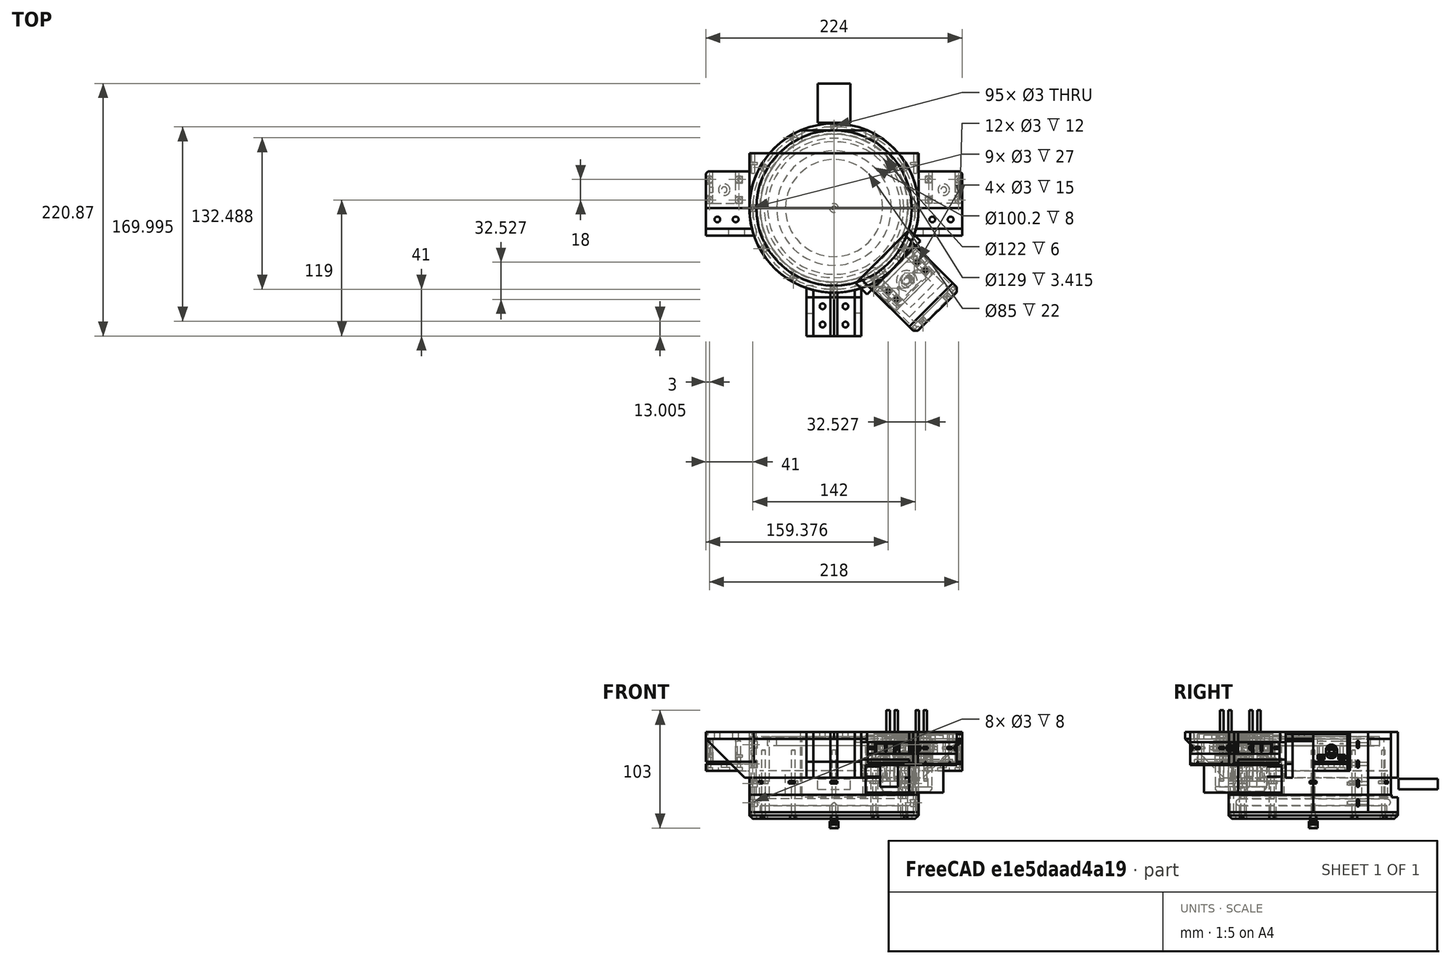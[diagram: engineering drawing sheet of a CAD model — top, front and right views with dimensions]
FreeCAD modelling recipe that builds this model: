
FCSTD DOCUMENT  (FreeCAD 0.19R24276 (Git))
Label: bazovina-part-H_turret-hole_049
License: All rights reserved
LicenseURL: http://en.wikipedia.org/wiki/All_rights_reserved
objects: Part::Cylinder×214, Part::Box×127, Part::Compound×119, Part::Cut×112, Part::Chamfer×32, Mesh::Feature×26, Part::FeaturePython×13, Part::Mirroring×4, Part::Common×2, Part::Torus×1
note: 624 computed .brp shape members not serialized (recipe doc carries the construction recipe); baked Part::Feature solids carry a one-line shape summary decoded from their .brp

FEATURE [Part::Box] Box485  label="Krychle485"
  AttacherType = Attacher::AttachEngine3D
  Height = 49
  Length = 56
  Placement = pos=(-28,35,29) rot=(0,0,1;0rad)
  Width = 200
FEATURE [Part::Box] Box486  label="Krychle486"
  AttacherType = Attacher::AttachEngine3D
  Height = 55
  Length = 148
  Placement = pos=(-74,68,29) rot=(0,0,1;0rad)
  Width = 26
FEATURE [Part::FeaturePython] Tube035  # WARN: FeaturePython — macro-defined, semantics opaque (R4)
  AttacherType = Attacher::AttachEngine3D
  Height = 55
  InnerRadius = 68
  OuterRadius = 74
  Placement = pos=(0,0,29) rot=(0,0,1;0rad)
FEATURE [Part::Cut] Cut455
  Base = -> Tube035
  Tool = -> Box485
FEATURE [Part::Cut] Cut454
  Base = -> Cut455
  Tool = -> Box486
FEATURE [Part::Cylinder] Cylinder971  label="Válec971"
  Angle = 360
  AttacherType = Attacher::AttachEngine3D
  Height = 6
  Placement = pos=(0,0,65) rot=(0,0,1;0rad)
  Radius = 74
FEATURE [Part::Box] Box483  label="Krychle483"
  AttacherType = Attacher::AttachEngine3D
  Height = 34
  Length = 148
  Placement = pos=(-74,68,38) rot=(0,0,1;0rad)
  Width = 20
FEATURE [Part::Cut] Cut453
  Base = -> Cylinder971
  Placement = pos=(0,0,13) rot=(0,0,1;0rad)
  Tool = -> Box483
FEATURE [Part::FeaturePython] Tube036  # WARN: FeaturePython — macro-defined, semantics opaque (R4)
  AttacherType = Attacher::AttachEngine3D
  Height = 8
  InnerRadius = 50.1
  OuterRadius = 58
  Placement = pos=(0,0,72) rot=(0,0,1;0rad)
FEATURE [Part::Box] Box648  label="Krychle648"
  AttacherType = Attacher::AttachEngine3D
  Height = 60
  Length = 200
  Placement = pos=(0,0,-5) rot=(0,0,-1;0.383972rad)
  Width = 200
FEATURE [Part::Box] Box647  label="Krychle647"
  AttacherType = Attacher::AttachEngine3D
  Height = 60
  Length = 200
  Placement = pos=(70.7107,70.7107,-5) rot=(0,0,1;3.92699rad)
  Width = 120
FEATURE [Part::Box] Box649  label="Krychle649"
  AttacherType = Attacher::AttachEngine3D
  Height = 60
  Length = 200
  Placement = pos=(0,0,-5) rot=(0,0,1;3.52556rad)
  Width = 200
FEATURE [Part::Cut] Cut464
  Base = -> Box647
  Tool = -> Box648
FEATURE [Part::Cut] Cut465
  Base = -> Cut464
  Tool = -> Box649
FEATURE [Part::Cut] Cut
  Base = -> Cut454
  Tool = -> Cut465
FEATURE [Part::Cylinder] Cylinder983  label="Válec983"
  Angle = 360
  AttacherType = Attacher::AttachEngine3D
  Height = 60
  Placement = pos=(-61.4878,-35.5,0) rot=(0,0,-1;1.0472rad)
  Radius = 1.5
FEATURE [Part::Cylinder] Cylinder978  label="Válec978"
  Angle = 360
  AttacherType = Attacher::AttachEngine3D
  Height = 60
  Placement = pos=(35.5,61.4878,0) rot=(0,0,1;2.61799rad)
  Radius = 1.5
FEATURE [Part::Cylinder] Cylinder981  label="Válec981"
  Angle = 360
  AttacherType = Attacher::AttachEngine3D
  Height = 60
  Placement = pos=(-61.4878,35.5,0) rot=(0,0,1;4.18879rad)
  Radius = 1.5
FEATURE [Part::Cylinder] Cylinder975  label="Válec975"
  Angle = 360
  AttacherType = Attacher::AttachEngine3D
  Height = 60
  Placement = pos=(61.4878,-35.5,0) rot=(0,0,1;1.0472rad)
  Radius = 1.5
FEATURE [Part::Cylinder] Cylinder986  label="Válec986"
  Angle = 360
  AttacherType = Attacher::AttachEngine3D
  Height = 3
  Placement = pos=(-71,2.7e-14,0) rot=(0,0,-1;1.5708rad)
  Radius = 3
FEATURE [Part::Cylinder] Cylinder980  label="Válec980"
  Angle = 360
  AttacherType = Attacher::AttachEngine3D
  Height = 60
  Placement = pos=(-35.5,61.4878,0) rot=(0,0,1;3.66519rad)
  Radius = 1.5
FEATURE [Part::Cylinder] Cylinder977  label="Válec977"
  Angle = 360
  AttacherType = Attacher::AttachEngine3D
  Height = 60
  Placement = pos=(61.4878,35.5,0) rot=(0,0,1;2.0944rad)
  Radius = 1.5
FEATURE [Part::Cylinder] Cylinder979  label="Válec979"
  Angle = 360
  AttacherType = Attacher::AttachEngine3D
  Height = 60
  Placement = pos=(3.1e-14,71,0) rot=(0,0,1;3.14159rad)
  Radius = 1.5
FEATURE [Part::Cylinder] Cylinder976  label="Válec976"
  Angle = 360
  AttacherType = Attacher::AttachEngine3D
  Height = 60
  Placement = pos=(71,-1.8e-14,0) rot=(0,0,1;1.5708rad)
  Radius = 1.5
FEATURE [Part::Cylinder] Cylinder982  label="Válec982"
  Angle = 360
  AttacherType = Attacher::AttachEngine3D
  Height = 60
  Placement = pos=(-71,2.7e-14,0) rot=(0,0,-1;1.5708rad)
  Radius = 1.5
FEATURE [Part::Cylinder] Cylinder973  label="Válec973"
  Angle = 360
  AttacherType = Attacher::AttachEngine3D
  Height = 60
  Placement = pos=(0,-71,0) rot=(0,0,1;0rad)
  Radius = 1.5
FEATURE [Part::Cylinder] Cylinder974  label="Válec974"
  Angle = 360
  AttacherType = Attacher::AttachEngine3D
  Height = 60
  Placement = pos=(35.5,-61.4878,0) rot=(0,0,1;0.523599rad)
  Radius = 1.5
FEATURE [Part::Compound] Compound525
  Links = -> [Cylinder973,Cylinder974,Cylinder975,Cylinder976,Cylinder977,Cylinder978,Cylinder979,Cylinder980,Cylinder981,Cylinder982,Cylinder983]
FEATURE [Part::Cylinder] Cylinder984  label="Válec984"
  Angle = 360
  AttacherType = Attacher::AttachEngine3D
  Height = 3
  Placement = pos=(35.5,61.4878,0) rot=(0,0,1;2.61799rad)
  Radius = 3
FEATURE [Part::Cylinder] Cylinder985  label="Válec985"
  Angle = 360
  AttacherType = Attacher::AttachEngine3D
  Height = 3
  Placement = pos=(-61.4878,35.5,0) rot=(0,0,1;4.18879rad)
  Radius = 3
FEATURE [Part::FeaturePython] Tube031  # WARN: FeaturePython — macro-defined, semantics opaque (R4)
  AttacherType = Attacher::AttachEngine3D
  Height = 6
  InnerRadius = 61
  OuterRadius = 74
  Placement = pos=(0,0,14) rot=(0,0,1;0rad)
FEATURE [Part::Cylinder] Cylinder991  label="Válec991"
  Angle = 360
  AttacherType = Attacher::AttachEngine3D
  Height = 3
  Placement = pos=(61.4878,-35.5,0) rot=(0,0,1;1.0472rad)
  Radius = 3
FEATURE [Part::Cylinder] Cylinder990  label="Válec990"
  Angle = 360
  AttacherType = Attacher::AttachEngine3D
  Height = 3
  Placement = pos=(35.5,-61.4878,0) rot=(0,0,1;0.523599rad)
  Radius = 3
FEATURE [Part::Cylinder] Cylinder993  label="Válec993"
  Angle = 360
  AttacherType = Attacher::AttachEngine3D
  Height = 3
  Placement = pos=(0,-71,0) rot=(0,0,1;0rad)
  Radius = 3
FEATURE [Part::Cylinder] Cylinder987  label="Válec987"
  Angle = 360
  AttacherType = Attacher::AttachEngine3D
  Height = 3
  Placement = pos=(71,-1.8e-14,0) rot=(0,0,1;1.5708rad)
  Radius = 3
FEATURE [Part::Cylinder] Cylinder992  label="Válec992"
  Angle = 360
  AttacherType = Attacher::AttachEngine3D
  Height = 3
  Placement = pos=(-61.4878,-35.5,0) rot=(0,0,-1;1.0472rad)
  Radius = 3
FEATURE [Part::Cylinder] Cylinder994  label="Válec994"
  Angle = 360
  AttacherType = Attacher::AttachEngine3D
  Height = 3
  Placement = pos=(-35.5,61.4878,0) rot=(0,0,1;3.66519rad)
  Radius = 3
FEATURE [Part::Cylinder] Cylinder988  label="Válec988"
  Angle = 360
  AttacherType = Attacher::AttachEngine3D
  Height = 3
  Placement = pos=(61.4878,35.5,0) rot=(0,0,1;2.0944rad)
  Radius = 3
FEATURE [Part::Cylinder] Cylinder989  label="Válec989"
  Angle = 360
  AttacherType = Attacher::AttachEngine3D
  Height = 3
  Placement = pos=(3.1e-14,71,0) rot=(0,0,1;3.14159rad)
  Radius = 3
FEATURE [Part::Compound] Compound526
  Links = -> [Cylinder993,Cylinder990,Cylinder991,Cylinder987,Cylinder988,Cylinder984,Cylinder989,Cylinder994,Cylinder985,Cylinder986,Cylinder992]
  Placement = pos=(0,0,17) rot=(0,0,1;0rad)
FEATURE [Part::Chamfer] Chamfer
  Base = -> Tube031
  Edges = 1 edges r=3: [Edge1]
FEATURE [Part::Cut] Cut207
  Base = -> Chamfer
  Tool = -> Compound526
FEATURE [Part::Cut] Cut208  label="bazovina_part-G_seal"
  Base = -> Cut207
  Placement = pos=(0,0,28) rot=(1,0,0;3.14159rad)
  Tool = -> Compound525
FEATURE [Part::Torus] Torus001  label="Anuloid001"
  Angle1 = -180
  Angle2 = 180
  Angle3 = 360
  AttacherType = Attacher::AttachEngine3D
  Placement = pos=(0,0,24.5) rot=(0,0,1;0rad)
  Radius1 = 64.2
  Radius2 = 3.1
FEATURE [Part::FeaturePython] Tube024  # WARN: FeaturePython — macro-defined, semantics opaque (R4)
  AttacherType = Attacher::AttachEngine3D
  Height = 15
  InnerRadius = 64.5
  OuterRadius = 74
  Placement = pos=(0,0,16) rot=(0,0,1;0rad)
FEATURE [Part::Cut] Cut466
  Base = -> Tube024
  Tool = -> Torus001
FEATURE [Part::Box] Box179  label="Krychle179"
  AttacherType = Attacher::AttachEngine3D
  Height = 47
  Length = 56
  Placement = pos=(-28,0,29) rot=(0,0,1;0rad)
  Width = 200
FEATURE [Part::Box] Box208  label="Krychle208"
  AttacherType = Attacher::AttachEngine3D
  Height = 6
  Length = 8
  Placement = pos=(67,38,21) rot=(0,0,1;0rad)
  Width = 2
FEATURE [Part::Cylinder] Cylinder510  label="Válec510"
  Angle = 360
  AttacherType = Attacher::AttachEngine3D
  Height = 50
  Placement = pos=(-71,80,24) rot=(1,0,0;1.5708rad)
  Radius = 1.5
FEATURE [Part::Cylinder] Cylinder509  label="Válec509"
  Angle = 360
  AttacherType = Attacher::AttachEngine3D
  Height = 50
  Placement = pos=(71,80,24) rot=(1,0,0;1.5708rad)
  Radius = 1.5
FEATURE [Part::Box] Box209  label="Krychle209"
  AttacherType = Attacher::AttachEngine3D
  Height = 6
  Length = 8
  Placement = pos=(-75,38,21) rot=(0,0,1;0rad)
  Width = 2
FEATURE [Part::Cylinder] Cylinder485  label="Válec485"
  Angle = 360
  AttacherType = Attacher::AttachEngine3D
  Height = 15
  Placement = pos=(0,0,16) rot=(0,0,1;0rad)
  Radius = 74
FEATURE [Part::Compound] Compound339
  Links = -> [Cylinder509,Cylinder510]
FEATURE [Part::Compound] Compound338
  Links = -> [Box208,Box209]
FEATURE [Part::Cylinder] Cylinder995  label="Válec995"
  Angle = 360
  AttacherType = Attacher::AttachEngine3D
  Height = 60
  Placement = pos=(61.4878,35.5,0) rot=(0,0,1;2.0944rad)
  Radius = 1.5
FEATURE [Part::Cylinder] Cylinder996  label="Válec996"
  Angle = 360
  AttacherType = Attacher::AttachEngine3D
  Height = 60
  Placement = pos=(35.5,-61.4878,0) rot=(0,0,1;0.523599rad)
  Radius = 1.5
FEATURE [Part::Cylinder] Cylinder997  label="Válec997"
  Angle = 360
  AttacherType = Attacher::AttachEngine3D
  Height = 60
  Placement = pos=(71,-1.8e-14,0) rot=(0,0,1;1.5708rad)
  Radius = 1.5
FEATURE [Part::Cylinder] Cylinder998  label="Válec998"
  Angle = 360
  AttacherType = Attacher::AttachEngine3D
  Height = 60
  Placement = pos=(35.5,61.4878,0) rot=(0,0,1;2.61799rad)
  Radius = 1.5
FEATURE [Part::Cylinder] Cylinder999  label="Válec999"
  Angle = 360
  AttacherType = Attacher::AttachEngine3D
  Height = 60
  Placement = pos=(-61.4878,35.5,0) rot=(0,0,1;4.18879rad)
  Radius = 1.5
FEATURE [Part::Cylinder] Cylinder1000  label="Válec1000"
  Angle = 360
  AttacherType = Attacher::AttachEngine3D
  Height = 60
  Placement = pos=(-71,2.7e-14,0) rot=(0,0,-1;1.5708rad)
  Radius = 1.5
FEATURE [Part::Cylinder] Cylinder1001  label="Válec1001"
  Angle = 360
  AttacherType = Attacher::AttachEngine3D
  Height = 60
  Placement = pos=(-61.4878,-35.5,0) rot=(0,0,-1;1.0472rad)
  Radius = 1.5
FEATURE [Part::Cylinder] Cylinder1002  label="Válec1002"
  Angle = 360
  AttacherType = Attacher::AttachEngine3D
  Height = 60
  Placement = pos=(-35.5,61.4878,0) rot=(0,0,1;3.66519rad)
  Radius = 1.5
FEATURE [Part::Cylinder] Cylinder1003  label="Válec1003"
  Angle = 360
  AttacherType = Attacher::AttachEngine3D
  Height = 60
  Placement = pos=(-35.5,-61.4878,0) rot=(0,0,-1;0.523599rad)
  Radius = 1.5
FEATURE [Part::Cylinder] Cylinder1004  label="Válec1004"
  Angle = 360
  AttacherType = Attacher::AttachEngine3D
  Height = 60
  Placement = pos=(61.4878,-35.5,0) rot=(0,0,1;1.0472rad)
  Radius = 1.5
FEATURE [Part::Cylinder] Cylinder1005  label="Válec1005"
  Angle = 360
  AttacherType = Attacher::AttachEngine3D
  Height = 60
  Placement = pos=(0,-71,0) rot=(0,0,1;0rad)
  Radius = 1.5
FEATURE [Part::Compound] Compound527
  Links = -> [Cylinder1005,Cylinder996,Cylinder1004,Cylinder997,Cylinder995,Cylinder998,Cylinder1002,Cylinder999,Cylinder1000,Cylinder1001,Cylinder1003]
FEATURE [Part::Box] Box176  label="Krychle176"
  AttacherType = Attacher::AttachEngine3D
  Height = 15
  Length = 148
  Placement = pos=(-74,0,16) rot=(0,0,1;0rad)
  Width = 48
FEATURE [Part::Cylinder] Cylinder476  label="Válec476"
  Angle = 360
  AttacherType = Attacher::AttachEngine3D
  Height = 20
  Placement = pos=(0,-63.8,4.5) rot=(0,0,1;0rad)
  Radius = 3.5
FEATURE [Part::Cut] Cut176
  Base = -> Cut466
  Tool = -> Cylinder476
FEATURE [Part::Cylinder] Cylinder482  label="Válec482"
  Angle = 360
  AttacherType = Attacher::AttachEngine3D
  Height = 15
  Placement = pos=(0,0,16) rot=(0,0,1;0rad)
  Radius = 74
FEATURE [Part::Cut] Cut185
  Base = -> Box176
  Tool = -> Cylinder482
FEATURE [Part::Cut] Cut188
  Base = -> Cut185
  Tool = -> Cylinder485
FEATURE [Part::Compound] Compound337
  Links = -> [Cut188,Cut176]
FEATURE [Part::Cut] Cut201
  Base = -> Compound337
  Tool = -> Compound338
FEATURE [Part::Cut] Cut202
  Base = -> Cut201
  Tool = -> Compound339
FEATURE [Part::Cut] Cut203
  Base = -> Cut202
  Tool = -> Box179
FEATURE [Part::Cut] Cut204  label="bazovina_part-E_lozo-okruh-novo"
  Base = -> Cut203
  Placement = pos=(0,0,-2) rot=(0,0,1;0rad)
  Tool = -> Compound527
FEATURE [Part::Cylinder] Cylinder1627  label="Válec1627"
  Angle = 360
  AttacherType = Attacher::AttachEngine3D
  Height = 50
  Placement = pos=(35.5,-61.49,11) rot=(0,0,1;0.523599rad)
  Radius = 3
FEATURE [Part::Cylinder] Cylinder1628  label="Válec1628"
  Angle = 360
  AttacherType = Attacher::AttachEngine3D
  Height = 50
  Placement = pos=(61.49,-35.5,11) rot=(0,0,1;1.0472rad)
  Radius = 3
FEATURE [Part::Box] Box488  label="Krychle488"
  AttacherType = Attacher::AttachEngine3D
  Height = 2
  Length = 6
  Placement = pos=(-3,-75,39) rot=(0,0,1;0rad)
  Width = 8
FEATURE [Part::Box] Box489  label="Krychle489"
  AttacherType = Attacher::AttachEngine3D
  Height = 2
  Length = 6
  Placement = pos=(34.9,-66.45,58) rot=(0,0,1;0.523599rad)
  Width = 8
FEATURE [Part::Box] Box497  label="Krychle497"
  AttacherType = Attacher::AttachEngine3D
  Height = 2
  Length = 6
  Placement = pos=(-75,3,39) rot=(0,0,-1;1.5708rad)
  Width = 8
FEATURE [Part::Box] Box493  label="Krychle493"
  AttacherType = Attacher::AttachEngine3D
  Height = 2
  Length = 6
  Placement = pos=(40.0981,63.4519,39) rot=(0,0,1;2.61799rad)
  Width = 8
FEATURE [Part::Box] Box491  label="Krychle491"
  AttacherType = Attacher::AttachEngine3D
  Height = 2
  Length = 6
  Placement = pos=(75,-3,39) rot=(0,0,1;1.5708rad)
  Width = 8
FEATURE [Part::Box] Box495  label="Krychle495"
  AttacherType = Attacher::AttachEngine3D
  Height = 2
  Length = 6
  Placement = pos=(-34.9019,66.4519,39) rot=(0,0,1;3.66519rad)
  Width = 8
FEATURE [Part::Box] Box490  label="Krychle490"
  AttacherType = Attacher::AttachEngine3D
  Height = 2
  Length = 6
  Placement = pos=(63.45,-40.1,58) rot=(0,0,1;1.0472rad)
  Width = 8
FEATURE [Part::Box] Box494  label="Krychle494"
  AttacherType = Attacher::AttachEngine3D
  Height = 2
  Length = 6
  Placement = pos=(3,75,39) rot=(0,0,1;3.14159rad)
  Width = 8
FEATURE [Part::Box] Box498  label="Krychle498"
  AttacherType = Attacher::AttachEngine3D
  Height = 2
  Length = 6
  Placement = pos=(-66.4519,-34.9019,39) rot=(0,0,-1;1.0472rad)
  Width = 8
FEATURE [Part::Box] Box492  label="Krychle492"
  AttacherType = Attacher::AttachEngine3D
  Height = 2
  Length = 6
  Placement = pos=(66.4519,34.9019,39) rot=(0,0,1;2.0944rad)
  Width = 8
FEATURE [Part::Box] Box499  label="Krychle499"
  AttacherType = Attacher::AttachEngine3D
  Height = 2
  Length = 6
  Placement = pos=(-40.0981,-63.4519,39) rot=(0,0,-1;0.523599rad)
  Width = 8
FEATURE [Part::Box] Box496  label="Krychle496"
  AttacherType = Attacher::AttachEngine3D
  Height = 2
  Length = 6
  Placement = pos=(-63.4519,40.0981,39) rot=(0,0,1;4.18879rad)
  Width = 8
FEATURE [Part::Compound] Compound528
  Links = -> [Box488,Box489,Box490,Box491,Box492,Box493,Box494,Box495,Box496,Box497,Box498,Box499]
FEATURE [Part::Cylinder] Cylinder1629  label="Válec1629"
  Angle = 360
  AttacherType = Attacher::AttachEngine3D
  Height = 72
  Placement = pos=(71,-1.8e-14,0) rot=(0,0,1;1.5708rad)
  Radius = 1.5
FEATURE [Part::Cylinder] Cylinder1630  label="Válec1630"
  Angle = 360
  AttacherType = Attacher::AttachEngine3D
  Height = 72
  Placement = pos=(35.5,61.4878,0) rot=(0,0,1;2.61799rad)
  Radius = 1.5
FEATURE [Part::Cylinder] Cylinder1631  label="Válec1631"
  Angle = 360
  AttacherType = Attacher::AttachEngine3D
  Height = 72
  Placement = pos=(61.4878,-35.5,0) rot=(0,0,1;1.0472rad)
  Radius = 1.5
FEATURE [Part::Cylinder] Cylinder1632  label="Válec1632"
  Angle = 360
  AttacherType = Attacher::AttachEngine3D
  Height = 72
  Placement = pos=(35.5,-61.4878,0) rot=(0,0,1;0.523599rad)
  Radius = 1.5
FEATURE [Part::Cylinder] Cylinder1633  label="Válec1633"
  Angle = 360
  AttacherType = Attacher::AttachEngine3D
  Height = 72
  Placement = pos=(-35.5,-61.4878,0) rot=(0,0,-1;0.523599rad)
  Radius = 1.5
FEATURE [Part::Cylinder] Cylinder1634  label="Válec1634"
  Angle = 360
  AttacherType = Attacher::AttachEngine3D
  Height = 72
  Placement = pos=(-71,2.7e-14,0) rot=(0,0,-1;1.5708rad)
  Radius = 1.5
FEATURE [Part::Cylinder] Cylinder1635  label="Válec1635"
  Angle = 360
  AttacherType = Attacher::AttachEngine3D
  Height = 72
  Placement = pos=(-61.4878,-35.5,0) rot=(0,0,-1;1.0472rad)
  Radius = 1.5
FEATURE [Part::Cylinder] Cylinder1636  label="Válec1636"
  Angle = 360
  AttacherType = Attacher::AttachEngine3D
  Height = 72
  Placement = pos=(61.4878,35.5,0) rot=(0,0,1;2.0944rad)
  Radius = 1.5
FEATURE [Part::Cylinder] Cylinder1637  label="Válec1637"
  Angle = 360
  AttacherType = Attacher::AttachEngine3D
  Height = 72
  Placement = pos=(0,-71,0) rot=(0,0,1;0rad)
  Radius = 1.5
FEATURE [Part::Cylinder] Cylinder1638  label="Válec1638"
  Angle = 360
  AttacherType = Attacher::AttachEngine3D
  Height = 72
  Placement = pos=(-35.5,61.4878,0) rot=(0,0,1;3.66519rad)
  Radius = 1.5
FEATURE [Part::Cylinder] Cylinder1639  label="Válec1639"
  Angle = 360
  AttacherType = Attacher::AttachEngine3D
  Height = 72
  Placement = pos=(-61.4878,35.5,0) rot=(0,0,1;4.18879rad)
  Radius = 1.5
FEATURE [Part::Cylinder] Cylinder1640  label="Válec1640"
  Angle = 360
  AttacherType = Attacher::AttachEngine3D
  Height = 72
  Placement = pos=(3.1e-14,71,0) rot=(0,0,1;3.14159rad)
  Radius = 1.5
FEATURE [Part::Compound] Compound529
  Links = -> [Cylinder1637,Cylinder1632,Cylinder1631,Cylinder1629,Cylinder1636,Cylinder1630,Cylinder1640,Cylinder1638,Cylinder1639,Cylinder1634,Cylinder1635,Cylinder1633]
  Placement = pos=(0,0,-4) rot=(0,0,1;0rad)
FEATURE [Part::Cylinder] Cylinder1626  label="Válec1626"
  Angle = 360
  AttacherType = Attacher::AttachEngine3D
  Height = 4
  Placement = pos=(0,90,53) rot=(0,0,1;0rad)
  Radius = 6
FEATURE [Part::Cylinder] Cylinder1622  label="Válec1622"
  Angle = 360
  AttacherType = Attacher::AttachEngine3D
  Height = 1
  Placement = pos=(0,90,72) rot=(0,0,1;0rad)
  Radius = 4
FEATURE [Part::Cylinder] Cylinder1623  label="Válec1623"
  Angle = 360
  AttacherType = Attacher::AttachEngine3D
  Height = 1
  Placement = pos=(0,90,62) rot=(0,0,1;0rad)
  Radius = 4
FEATURE [Part::Cylinder] Cylinder1625  label="Válec1625"
  Angle = 360
  AttacherType = Attacher::AttachEngine3D
  Height = 5
  Placement = pos=(0,90,57) rot=(0,0,1;0rad)
  Radius = 5
FEATURE [Part::Cylinder] Cylinder1624  label="Válec1624"
  Angle = 360
  AttacherType = Attacher::AttachEngine3D
  Height = 5
  Placement = pos=(0,90,73) rot=(0,0,1;0rad)
  Radius = 5
FEATURE [Part::Compound] Compound808
  Links = -> [Cylinder1624,Cylinder1625,Cylinder1622,Cylinder1623,Cylinder1626]
  Placement = pos=(0,0,4) rot=(0,0,1;3.92699rad)
FEATURE [Part::Cylinder] Cylinder1641  label="Válec1641"
  Angle = 360
  AttacherType = Attacher::AttachEngine3D
  Height = 9
  Placement = pos=(35.5,-61.49,45) rot=(0,0,1;0.523599rad)
  Radius = 9
FEATURE [Part::Cylinder] Cylinder1642  label="Válec1642"
  Angle = 360
  AttacherType = Attacher::AttachEngine3D
  Height = 9
  Placement = pos=(61.49,-35.5,45) rot=(0,0,1;1.0472rad)
  Radius = 9
FEATURE [Part::Cut] Cut467
  Base = -> Cut
  Tool = -> Compound528
FEATURE [Part::Cut] Cut468
  Base = -> Cut467
  Tool = -> Compound529
FEATURE [Part::Box] Box646  label="Krychle646"
  AttacherType = Attacher::AttachEngine3D
  Height = 9
  Length = 28.8
  Placement = pos=(-14.4,-14,34) rot=(0,0,1;0rad)
  Width = 34.4
FEATURE [Part::Compound] Compound804
  Links = -> [Box646]
  Placement = pos=(63.64,-63.64,33) rot=(0,0,1;3.92699rad)
FEATURE [Part::Box] Box650  label="Krychle650"
  AttacherType = Attacher::AttachEngine3D
  Height = 9
  Length = 28.8
  Placement = pos=(-14.4,-15.34,34) rot=(0,0,1;0rad)
  Width = 34.21
FEATURE [Part::Compound] Compound
  Links = -> [Box650]
  Placement = pos=(0,90,0) rot=(0,0,1;0rad)
FEATURE [Part::Box] Box651  label="Krychle651"
  AttacherType = Attacher::AttachEngine3D
  Height = 9
  Length = 42
  Placement = pos=(-21,-12,34) rot=(0,0,1;0rad)
  Width = 24
FEATURE [Part::Compound] Compound809
  Links = -> [Box651]
  Placement = pos=(63.64,-63.64,33) rot=(0,0,1;3.92699rad)
FEATURE [Part::Box] Box652  label="Krychle652"
  AttacherType = Attacher::AttachEngine3D
  Height = 9
  Length = 28.8
  Placement = pos=(-14.4,-15.34,34) rot=(0,0,1;0rad)
  Width = 34.21
FEATURE [Part::Compound] Compound810
  Links = -> [Box652]
  Placement = pos=(0,90,0) rot=(0,0,1;0rad)
FEATURE [Part::Cut] Cut469
  Base = -> Compound809
  Tool = -> Compound804
FEATURE [Part::Box] Box653  label="Krychle653"
  AttacherType = Attacher::AttachEngine3D
  Height = 1
  Length = 54
  Placement = pos=(-27,-12,34) rot=(0,0,1;0rad)
  Width = 24
FEATURE [Part::Compound] Compound811
  Links = -> [Box653]
  Placement = pos=(63.64,-63.64,42) rot=(0,0,1;3.92699rad)
FEATURE [Part::Cylinder] Cylinder1643  label="Válec1643"
  Angle = 360
  AttacherType = Attacher::AttachEngine3D
  Height = 1
  Placement = pos=(63.64,-63.64,76) rot=(0,0,1;3.92699rad)
  Radius = 4
FEATURE [Part::Cut] Cut470
  Base = -> Compound811
  Tool = -> Cylinder1643
FEATURE [Part::Box] Box654  label="Krychle654"
  AttacherType = Attacher::AttachEngine3D
  Height = 9
  Length = 42
  Placement = pos=(-21,-15.34,34) rot=(0,0,1;0rad)
  Width = 24
FEATURE [Part::Compound] Compound812
  Links = -> [Box654]
  Placement = pos=(63.64,-63.64,33) rot=(0,0,1;3.92699rad)
FEATURE [Part::Box] Box655  label="Krychle655"
  AttacherType = Attacher::AttachEngine3D
  Height = 9
  Length = 28.8
  Placement = pos=(-14.4,-15.34,34) rot=(0,0,1;0rad)
  Width = 34.21
FEATURE [Part::Compound] Compound813
  Links = -> [Box655]
  Placement = pos=(63.64,-63.64,33) rot=(0,0,1;3.92699rad)
FEATURE [Part::FeaturePython] Tube  # WARN: FeaturePython — macro-defined, semantics opaque (R4)
  AttacherType = Attacher::AttachEngine3D
  Height = 1
  InnerRadius = 4
  OuterRadius = 5
  Placement = pos=(0,90,81) rot=(0,0,1;0rad)
FEATURE [Part::Compound] Compound814
  Links = -> [Tube]
  Placement = pos=(0,0,0) rot=(0,0,1;3.92699rad)
FEATURE [Part::Box] Box656  label="Krychle656"
  AttacherType = Attacher::AttachEngine3D
  Height = 7
  Length = 42
  Placement = pos=(-21,-12,34) rot=(0,0,1;0rad)
  Width = 24
FEATURE [Part::Compound] Compound815
  Links = -> [Box656]
  Placement = pos=(63.64,-63.64,43) rot=(0,0,1;3.92699rad)
FEATURE [Part::Cylinder] Cylinder1644  label="Válec1644"
  Angle = 360
  AttacherType = Attacher::AttachEngine3D
  Height = 5
  Placement = pos=(0,90,77) rot=(0,0,1;0rad)
  Radius = 5
FEATURE [Part::Compound] Compound816
  Links = -> [Cylinder1644]
  Placement = pos=(0,0,0) rot=(0,0,1;3.92699rad)
FEATURE [Part::Cut] Cut471
  Base = -> Compound815
  Tool = -> Compound816
FEATURE [Part::Compound] Compound817
  Links = -> [Compound814,Cut471]
FEATURE [Part::Box] Box657  label="Krychle657"
  AttacherType = Attacher::AttachEngine3D
  Height = 2
  Length = 42
  Placement = pos=(-21,-12,34) rot=(0,0,1;0rad)
  Width = 24
FEATURE [Part::Compound] Compound818
  Links = -> [Box657]
  Placement = pos=(63.64,-63.64,42) rot=(0,0,1;3.92699rad)
FEATURE [Part::Cylinder] Cylinder1645  label="Válec1645"
  Angle = 360
  AttacherType = Attacher::AttachEngine3D
  Height = 4
  Placement = pos=(63.64,-63.64,76) rot=(0,0,1;3.92699rad)
  Radius = 4
FEATURE [Part::Cut] Cut472
  Base = -> Compound818
  Placement = pos=(0,0,-10) rot=(0,0,1;0rad)
  Tool = -> Cylinder1645
FEATURE [Part::Box] Box658  label="Krychle658"
  AttacherType = Attacher::AttachEngine3D
  Height = 7
  Length = 42
  Placement = pos=(-21,-12,34) rot=(0,0,1;0rad)
  Width = 24
FEATURE [Part::Cylinder] Cylinder1646  label="Válec1646"
  Angle = 360
  AttacherType = Attacher::AttachEngine3D
  Height = 5
  Placement = pos=(0,90,77) rot=(0,0,1;0rad)
  Radius = 5
FEATURE [Part::Compound] Compound819
  Links = -> [Box658]
  Placement = pos=(63.64,-63.64,43) rot=(0,0,1;3.92699rad)
FEATURE [Part::Compound] Compound820
  Links = -> [Cylinder1646]
  Placement = pos=(0,0,2) rot=(0,0,1;3.92699rad)
FEATURE [Part::Cut] Cut473
  Base = -> Compound819
  Placement = pos=(0,0,-22) rot=(0,0,1;0rad)
  Tool = -> Compound820
FEATURE [Part::Cylinder] Cylinder1647  label="Válec1647"
  Angle = 360
  AttacherType = Attacher::AttachEngine3D
  Height = 5
  Placement = pos=(0,90,77) rot=(0,0,1;0rad)
  Radius = 3
FEATURE [Part::Compound] Compound821
  Links = -> [Cylinder1647]
  Placement = pos=(0,0,-24) rot=(0,0,1;3.92699rad)
FEATURE [Part::Cut] Cut474
  Base = -> Cut473
  Tool = -> Compound821
FEATURE [Part::FeaturePython] Tube037  # WARN: FeaturePython — macro-defined, semantics opaque (R4)
  AttacherType = Attacher::AttachEngine3D
  Height = 1
  InnerRadius = 4
  OuterRadius = 5
  Placement = pos=(0,90,81) rot=(0,0,1;0rad)
FEATURE [Part::Compound] Compound822
  Links = -> [Tube037]
  Placement = pos=(0,0,-24) rot=(0,0,1;3.92699rad)
FEATURE [Part::Compound] Compound823
  Links = -> [Compound822,Cut474]
  Placement = pos=(0,0,4) rot=(0,0,1;0rad)
FEATURE [Part::Box] Box659  label="Krychle659"
  AttacherType = Attacher::AttachEngine3D
  Height = 9
  Length = 42
  Placement = pos=(-21,-14,34) rot=(0,0,1;0rad)
  Width = 28
FEATURE [Part::Compound] Compound824
  Links = -> [Box659]
  Placement = pos=(63.64,-63.64,33) rot=(0,0,1;3.92699rad)
FEATURE [Part::Box] Box660  label="Krychle660"
  AttacherType = Attacher::AttachEngine3D
  Height = 9
  Length = 54
  Placement = pos=(-27,-12,34) rot=(0,0,1;0rad)
  Width = 24
FEATURE [Part::Compound] Compound825
  Links = -> [Box660]
  Placement = pos=(63.64,-63.64,33) rot=(0,0,1;3.92699rad)
FEATURE [Part::Cut] Cut475
  Base = -> Compound825
  Tool = -> Compound824
FEATURE [Part::Cylinder] Cylinder1670  label="Válec1670"
  Angle = 360
  AttacherType = Attacher::AttachEngine3D
  Height = 20
  Placement = pos=(15.75,114,39.48) rot=(0,0.707107,0.707107;3.14159rad)
  Radius = 1.5
FEATURE [Part::Cylinder] Cylinder1671  label="Válec1671"
  Angle = 360
  AttacherType = Attacher::AttachEngine3D
  Height = 20
  Placement = pos=(15.75,114,58.525) rot=(0,0.707107,0.707107;3.14159rad)
  Radius = 1.5
FEATURE [Part::Compound] Compound826
  Links = -> [Cylinder1670,Cylinder1671]
  Placement = pos=(-49,0,-96) rot=(0.57735,0.57735,0.57735;2.0944rad)
FEATURE [Part::Compound] Compound827
  Links = -> [Compound826]
  Placement = pos=(52.33,-52.33,52) rot=(0,0,1;3.92699rad)
FEATURE [Part::Cylinder] Cylinder1672  label="Válec1672"
  Angle = 360
  AttacherType = Attacher::AttachEngine3D
  Height = 20
  Placement = pos=(15.75,114,39.48) rot=(0,0.707107,0.707107;3.14159rad)
  Radius = 1.5
FEATURE [Part::Cylinder] Cylinder1673  label="Válec1673"
  Angle = 360
  AttacherType = Attacher::AttachEngine3D
  Height = 20
  Placement = pos=(15.75,114,58.525) rot=(0,0.707107,0.707107;3.14159rad)
  Radius = 1.5
FEATURE [Part::Compound] Compound828
  Links = -> [Cylinder1672,Cylinder1673]
  Placement = pos=(-49,0,-96) rot=(0.57735,0.57735,0.57735;2.0944rad)
FEATURE [Part::Compound] Compound829
  Links = -> [Compound828]
  Placement = pos=(52.33,-52.33,52) rot=(0,0,1;3.92699rad)
FEATURE [Part::Cut] Cut476
  Base = -> Compound817
  Tool = -> Compound829
FEATURE [Part::Cut] Cut477
  Base = -> Cut470
  Tool = -> Compound827
FEATURE [Part::Box] Box661  label="Krychle661"
  AttacherType = Attacher::AttachEngine3D
  Height = 2
  Length = 6
  Placement = pos=(15,82,-56) rot=(0,0,1;0rad)
  Width = 6
FEATURE [Part::Box] Box662  label="Krychle662"
  AttacherType = Attacher::AttachEngine3D
  Height = 2
  Length = 6
  Placement = pos=(-21,82,-56) rot=(0,0,1;0rad)
  Width = 6
FEATURE [Part::Box] Box663  label="Krychle663"
  AttacherType = Attacher::AttachEngine3D
  Height = 2
  Length = 6
  Placement = pos=(-21,92,-56) rot=(0,0,1;0rad)
  Width = 6
FEATURE [Part::Box] Box664  label="Krychle664"
  AttacherType = Attacher::AttachEngine3D
  Height = 2
  Length = 6
  Placement = pos=(15,92,-56) rot=(0,0,1;0rad)
  Width = 6
FEATURE [Part::Compound] Compound807
  Links = -> [Box662,Box663,Box661,Box664]
  Placement = pos=(0,0,117) rot=(0,0,1;3.92699rad)
FEATURE [Part::Cylinder] Cylinder1621  label="Válec1621"
  Angle = 360
  AttacherType = Attacher::AttachEngine3D
  Height = 60
  Placement = pos=(18,95,-57) rot=(0,0,1;0rad)
  Radius = 1.5
FEATURE [Part::Cylinder] Cylinder1674  label="Válec1674"
  Angle = 360
  AttacherType = Attacher::AttachEngine3D
  Height = 60
  Placement = pos=(18,85,-57) rot=(0,0,1;0rad)
  Radius = 1.5
FEATURE [Part::Cylinder] Cylinder1675  label="Válec1675"
  Angle = 360
  AttacherType = Attacher::AttachEngine3D
  Height = 60
  Placement = pos=(-18,85,-57) rot=(0,0,1;0rad)
  Radius = 1.5
FEATURE [Part::Cylinder] Cylinder1676  label="Válec1676"
  Angle = 360
  AttacherType = Attacher::AttachEngine3D
  Height = 60
  Placement = pos=(-18,95,-57) rot=(0,0,1;0rad)
  Radius = 1.5
FEATURE [Part::Compound] Compound806
  Links = -> [Cylinder1621,Cylinder1674,Cylinder1675,Cylinder1676]
  Placement = pos=(0,0,100) rot=(0,0,1;3.92699rad)
FEATURE [Part::Cylinder] Cylinder1677  label="Válec1677"
  Angle = 360
  AttacherType = Attacher::AttachEngine3D
  Height = 3
  Placement = pos=(-18,85,-57) rot=(0,0,1;0rad)
  Radius = 3
FEATURE [Part::Cylinder] Cylinder1678  label="Válec1678"
  Angle = 360
  AttacherType = Attacher::AttachEngine3D
  Height = 3
  Placement = pos=(-18,95,-57) rot=(0,0,1;0rad)
  Radius = 3
FEATURE [Part::Cylinder] Cylinder1679  label="Válec1679"
  Angle = 360
  AttacherType = Attacher::AttachEngine3D
  Height = 3
  Placement = pos=(18,95,-57) rot=(0,0,1;0rad)
  Radius = 3
FEATURE [Part::Cylinder] Cylinder1680  label="Válec1680"
  Angle = 360
  AttacherType = Attacher::AttachEngine3D
  Height = 3
  Placement = pos=(18,85,-57) rot=(0,0,1;0rad)
  Radius = 3
FEATURE [Part::Compound] Compound830
  Links = -> [Cylinder1679,Cylinder1680,Cylinder1677,Cylinder1678]
  Placement = pos=(0,0,138) rot=(0,0,1;3.92699rad)
FEATURE [Part::Cylinder] Cylinder1681  label="Válec1681"
  Angle = 360
  AttacherType = Attacher::AttachEngine3D
  Height = 60
  Placement = pos=(-18,85,-57) rot=(0,0,1;0rad)
  Radius = 1.5
FEATURE [Part::Cylinder] Cylinder1682  label="Válec1682"
  Angle = 360
  AttacherType = Attacher::AttachEngine3D
  Height = 60
  Placement = pos=(-18,95,-57) rot=(0,0,1;0rad)
  Radius = 1.5
FEATURE [Part::Cylinder] Cylinder1683  label="Válec1683"
  Angle = 360
  AttacherType = Attacher::AttachEngine3D
  Height = 60
  Placement = pos=(18,95,-57) rot=(0,0,1;0rad)
  Radius = 1.5
FEATURE [Part::Cylinder] Cylinder1684  label="Válec1684"
  Angle = 360
  AttacherType = Attacher::AttachEngine3D
  Height = 60
  Placement = pos=(18,85,-57) rot=(0,0,1;0rad)
  Radius = 1.5
FEATURE [Part::Compound] Compound831
  Links = -> [Cylinder1683,Cylinder1684,Cylinder1681,Cylinder1682]
  Placement = pos=(0,0,100) rot=(0,0,1;3.92699rad)
FEATURE [Part::Cylinder] Cylinder1685  label="Válec1685"
  Angle = 360
  AttacherType = Attacher::AttachEngine3D
  Height = 60
  Placement = pos=(-18,85,-57) rot=(0,0,1;0rad)
  Radius = 1.5
FEATURE [Part::Cylinder] Cylinder1686  label="Válec1686"
  Angle = 360
  AttacherType = Attacher::AttachEngine3D
  Height = 60
  Placement = pos=(-18,95,-57) rot=(0,0,1;0rad)
  Radius = 1.5
FEATURE [Part::Cylinder] Cylinder1687  label="Válec1687"
  Angle = 360
  AttacherType = Attacher::AttachEngine3D
  Height = 60
  Placement = pos=(18,95,-57) rot=(0,0,1;0rad)
  Radius = 1.5
FEATURE [Part::Cylinder] Cylinder1688  label="Válec1688"
  Angle = 360
  AttacherType = Attacher::AttachEngine3D
  Height = 60
  Placement = pos=(18,85,-57) rot=(0,0,1;0rad)
  Radius = 1.5
FEATURE [Part::Compound] Compound832
  Links = -> [Cylinder1687,Cylinder1688,Cylinder1685,Cylinder1686]
  Placement = pos=(0,0,100) rot=(0,0,1;3.92699rad)
FEATURE [Part::Cut] Cut480
  Base = -> Cut477
  Tool = -> Compound831
FEATURE [Part::Cylinder] Cylinder1689  label="Válec1689"
  Angle = 360
  AttacherType = Attacher::AttachEngine3D
  Height = 60
  Placement = pos=(-18,85,-57) rot=(0,0,1;0rad)
  Radius = 1.5
FEATURE [Part::Cylinder] Cylinder1690  label="Válec1690"
  Angle = 360
  AttacherType = Attacher::AttachEngine3D
  Height = 60
  Placement = pos=(-18,95,-57) rot=(0,0,1;0rad)
  Radius = 1.5
FEATURE [Part::Cylinder] Cylinder1691  label="Válec1691"
  Angle = 360
  AttacherType = Attacher::AttachEngine3D
  Height = 60
  Placement = pos=(18,95,-57) rot=(0,0,1;0rad)
  Radius = 1.5
FEATURE [Part::Cylinder] Cylinder1692  label="Válec1692"
  Angle = 360
  AttacherType = Attacher::AttachEngine3D
  Height = 60
  Placement = pos=(18,85,-57) rot=(0,0,1;0rad)
  Radius = 1.5
FEATURE [Part::Compound] Compound833
  Links = -> [Cylinder1691,Cylinder1692,Cylinder1689,Cylinder1690]
  Placement = pos=(0,0,100) rot=(0,0,1;3.92699rad)
FEATURE [Part::Cut] Cut481  label="Base_encoder-washer1"
  Base = -> Cut472
  Placement = pos=(0,0,-3) rot=(0,0,1;0rad)
  Tool = -> Compound833
FEATURE [Part::Cylinder] Cylinder1693  label="Válec1693"
  Angle = 360
  AttacherType = Attacher::AttachEngine3D
  Height = 60
  Placement = pos=(-18,85,-57) rot=(0,0,1;0rad)
  Radius = 1.5
FEATURE [Part::Cylinder] Cylinder1694  label="Válec1694"
  Angle = 360
  AttacherType = Attacher::AttachEngine3D
  Height = 60
  Placement = pos=(-18,95,-57) rot=(0,0,1;0rad)
  Radius = 1.5
FEATURE [Part::Cylinder] Cylinder1695  label="Válec1695"
  Angle = 360
  AttacherType = Attacher::AttachEngine3D
  Height = 60
  Placement = pos=(18,95,-57) rot=(0,0,1;0rad)
  Radius = 1.5
FEATURE [Part::Cylinder] Cylinder1696  label="Válec1696"
  Angle = 360
  AttacherType = Attacher::AttachEngine3D
  Height = 60
  Placement = pos=(18,85,-57) rot=(0,0,1;0rad)
  Radius = 1.5
FEATURE [Part::Compound] Compound834
  Links = -> [Cylinder1695,Cylinder1696,Cylinder1693,Cylinder1694]
  Placement = pos=(0,0,100) rot=(0,0,1;3.92699rad)
FEATURE [Part::Cut] Cut482
  Base = -> Compound823
  Tool = -> Compound834
FEATURE [Part::Compound] Compound835
  Links = -> [Cut469,Cut475]
FEATURE [Part::Cut] Cut483
  Base = -> Compound835
  Tool = -> Compound806
FEATURE [Part::Compound] Compound836  label="Base_encoder-sidehold2"
  Links = -> [Cut483,Cut480]
FEATURE [Part::Box] Box  label="Krychle"
  AttacherType = Attacher::AttachEngine3D
  Height = 6
  Length = 6
  Placement = pos=(21,90,69) rot=(0,0,1;0rad)
  Width = 2
FEATURE [Part::Compound] Compound837
  Links = -> [Box]
  Placement = pos=(0,0,0) rot=(0,0,1;3.92699rad)
FEATURE [Part::Box] Box665  label="Krychle665"
  AttacherType = Attacher::AttachEngine3D
  Height = 6
  Length = 6
  Placement = pos=(-27,90,69) rot=(0,0,1;0rad)
  Width = 2
FEATURE [Part::Compound] Compound838
  Links = -> [Box665]
  Placement = pos=(0,0,0) rot=(0,0,1;3.92699rad)
FEATURE [Part::Cylinder] Cylinder  label="Válec"
  Angle = 360
  AttacherType = Attacher::AttachEngine3D
  Height = 100
  Placement = pos=(-24,110,72) rot=(1,0,0;1.5708rad)
  Radius = 1.5
FEATURE [Part::Compound] Compound839
  Links = -> [Cylinder]
  Placement = pos=(0,0,0) rot=(0,0,1;3.92699rad)
FEATURE [Part::Cylinder] Cylinder1697  label="Válec1697"
  Angle = 360
  AttacherType = Attacher::AttachEngine3D
  Height = 100
  Placement = pos=(24,110,72) rot=(1,0,0;1.5708rad)
  Radius = 1.5
FEATURE [Part::Compound] Compound840
  Links = -> [Cylinder1697]
  Placement = pos=(0,0,0) rot=(0,0,1;3.92699rad)
FEATURE [Part::Compound] Compound841
  Links = -> [Compound837,Compound838]
FEATURE [Part::Compound] Compound842
  Links = -> [Compound839,Compound840]
FEATURE [Part::Cut] Cut484
  Base = -> Compound836
  Tool = -> Compound841
FEATURE [Part::Cut] Cut485  label="Base_encoder-sidehold004"
  Base = -> Cut484
  Tool = -> Compound842
FEATURE [Part::Box] Box666  label="Krychle666"
  AttacherType = Attacher::AttachEngine3D
  Height = 20
  Length = 28.8
  Placement = pos=(-14.4,-15.34,34) rot=(0,0,1;0rad)
  Width = 34.21
FEATURE [Part::Compound] Compound805
  Links = -> [Box666]
  Placement = pos=(0,90,-83) rot=(0,0,1;0rad)
FEATURE [Part::Box] Box667  label="Krychle667"
  AttacherType = Attacher::AttachEngine3D
  Height = 24
  Length = 42
  Placement = pos=(-21,78,-49) rot=(0,0,1;0rad)
  Width = 24
FEATURE [Part::Cylinder] Cylinder1698  label="Válec1698"
  Angle = 360
  AttacherType = Attacher::AttachEngine3D
  Height = 48
  Placement = pos=(0,90,-55) rot=(0,0,1;0rad)
  Radius = 2.5
FEATURE [Part::Cut] Cut315
  Base = -> Box667
  Placement = pos=(0,0,21) rot=(0,0,1;0rad)
  Tool = -> Compound805
FEATURE [Part::Cut] Cut316
  Base = -> Cut315
  Tool = -> Cylinder1698
FEATURE [Part::Chamfer] Chamfer038
  Base = -> Cut316
  Edges = 2 edges r=6: [Edge6,Edge8]
FEATURE [Part::Cylinder] Cylinder1699  label="Válec1699"
  Angle = 360
  AttacherType = Attacher::AttachEngine3D
  Height = 60
  Placement = pos=(18,95,-57) rot=(0,0,1;0rad)
  Radius = 1.5
FEATURE [Part::Cylinder] Cylinder1700  label="Válec1700"
  Angle = 360
  AttacherType = Attacher::AttachEngine3D
  Height = 60
  Placement = pos=(18,85,-57) rot=(0,0,1;0rad)
  Radius = 1.5
FEATURE [Part::Cylinder] Cylinder1701  label="Válec1701"
  Angle = 360
  AttacherType = Attacher::AttachEngine3D
  Height = 60
  Placement = pos=(-18,85,-57) rot=(0,0,1;0rad)
  Radius = 1.5
FEATURE [Part::Cylinder] Cylinder1702  label="Válec1702"
  Angle = 360
  AttacherType = Attacher::AttachEngine3D
  Height = 60
  Placement = pos=(-18,95,-57) rot=(0,0,1;0rad)
  Radius = 1.5
FEATURE [Part::Compound] Compound843
  Links = -> [Cylinder1699,Cylinder1700,Cylinder1701,Cylinder1702]
  Placement = pos=(0,0,-16) rot=(0,0,1;0rad)
FEATURE [Part::Cut] Cut325
  Base = -> Chamfer038
  Tool = -> Compound843
FEATURE [Part::Chamfer] Chamfer039
  Base = -> Cut325
  Edges = 2 edges r=4: [Edge17,Edge20]
FEATURE [Part::Chamfer] Chamfer044
  Base = -> Chamfer039
  Edges = 2 edges r=2: [Edge14,Edge35]
  Placement = pos=(0,0,31) rot=(0.92388,0.382683,0;3.14159rad)
FEATURE [Part::Cut] Cut486
  Base = -> Cut482
  Tool = -> Compound807
FEATURE [Part::Cylinder] Cylinder1703  label="Válec1703"
  Angle = 360
  AttacherType = Attacher::AttachEngine3D
  Height = 60
  Placement = pos=(-18,85,-57) rot=(0,0,1;0rad)
  Radius = 1.5
FEATURE [Part::Cylinder] Cylinder1704  label="Válec1704"
  Angle = 360
  AttacherType = Attacher::AttachEngine3D
  Height = 60
  Placement = pos=(-18,95,-57) rot=(0,0,1;0rad)
  Radius = 1.5
FEATURE [Part::Cylinder] Cylinder1705  label="Válec1705"
  Angle = 360
  AttacherType = Attacher::AttachEngine3D
  Height = 60
  Placement = pos=(18,95,-57) rot=(0,0,1;0rad)
  Radius = 1.5
FEATURE [Part::Cylinder] Cylinder1706  label="Válec1706"
  Angle = 360
  AttacherType = Attacher::AttachEngine3D
  Height = 60
  Placement = pos=(18,85,-57) rot=(0,0,1;0rad)
  Radius = 1.5
FEATURE [Part::Compound] Compound844
  Links = -> [Cylinder1705,Cylinder1706,Cylinder1703,Cylinder1704]
  Placement = pos=(0,0,100) rot=(0,0,1;3.92699rad)
FEATURE [Part::Cut] Cut487
  Base = -> Cut476
  Tool = -> Compound830
FEATURE [Part::Cut] Cut488
  Base = -> Cut487
  Tool = -> Compound844
FEATURE [Part::Chamfer] Chamfer045
  Base = -> Cut486
  Edges = 2 edges r=2: [Edge10,Edge36]
FEATURE [Part::Compound] Compound845  label="Base_encoder-uphold"
  Links = -> [Chamfer044,Chamfer045]
  Placement = pos=(0,0,-3) rot=(0,0,1;0rad)
FEATURE [Part::Chamfer] Chamfer047
  Base = -> Cut488
  Edges = 2 edges r=3: [Edge11,Edge39]
FEATURE [Part::Chamfer] Chamfer048  label="Base_encoder-bottomhold"
  Base = -> Chamfer047
  Edges = 2 edges r=3: [Edge6,Edge23]
  Placement = pos=(0,0,-2) rot=(0,0,1;0rad)
FEATURE [Part::Chamfer] Chamfer049
  Base = -> Cut485
  Edges = 4 edges r=1: [Edge48,Edge82,Edge99,Edge114]
FEATURE [Part::Chamfer] Chamfer050
  Base = -> Chamfer049
  Edges = 2 edges r=1: [Edge3,Edge68]
FEATURE [Part::Chamfer] Chamfer051  label="Base_encoder-sidehold"
  Base = -> Chamfer050
  Edges = 2 edges r=1: [Edge69,Edge97]
  Placement = pos=(0,0,-2) rot=(0,0,1;0rad)
FEATURE [Part::Cylinder] Cylinder1707  label="Válec1707"
  Angle = 360
  AttacherType = Attacher::AttachEngine3D
  Height = 40
  Placement = pos=(0,0,44) rot=(0,0,1;0rad)
  Radius = 74
FEATURE [Part::Box] Box668  label="Krychle668"
  AttacherType = Attacher::AttachEngine3D
  Height = 5
  Length = 54
  Placement = pos=(61.52,-23.33,55) rot=(0,0,1;3.92699rad)
  Width = 60
FEATURE [Part::Box] Box669  label="Krychle669"
  AttacherType = Attacher::AttachEngine3D
  Height = 50
  Length = 42
  Placement = pos=(57.28,-27.58,31) rot=(0,0,1;3.92699rad)
  Width = 54
FEATURE [Part::Box] Box670  label="Krychle670"
  AttacherType = Attacher::AttachEngine3D
  Height = 9
  Length = 54
  Placement = pos=(61.52,-23.33,75) rot=(0,0,1;3.92699rad)
  Width = 60
FEATURE [Part::Box] Box671  label="Krychle671"
  AttacherType = Attacher::AttachEngine3D
  Height = 50
  Length = 42
  Placement = pos=(-21.0011,60.0051,31) rot=(0,0,1;0rad)
  Width = 62
FEATURE [Part::Box] Box672  label="Krychle672"
  AttacherType = Attacher::AttachEngine3D
  Height = 9
  Length = 54
  Placement = pos=(-27.0044,59.998,75) rot=(0,0,1;0rad)
  Width = 68
FEATURE [Part::Compound] Compound846
  Links = -> [Box671]
  Placement = pos=(0,0,1) rot=(0,0,1;3.92699rad)
FEATURE [Part::Compound] Compound847
  Links = -> [Box672]
  Placement = pos=(0,0,0) rot=(0,0,1;3.92699rad)
FEATURE [Part::Cut] Cut489
  Base = -> Compound847
  Tool = -> Compound846
FEATURE [Part::Cylinder] Cylinder1708  label="Válec1708"
  Angle = 360
  AttacherType = Attacher::AttachEngine3D
  Height = 40
  Placement = pos=(0,0,44) rot=(0,0,1;0rad)
  Radius = 74
FEATURE [Part::Cut] Cut490
  Base = -> Cut489
  Tool = -> Cylinder1708
FEATURE [Part::Box] Box673  label="Krychle673"
  AttacherType = Attacher::AttachEngine3D
  Height = 10
  Length = 54
  Placement = pos=(-27.0044,59.998,75) rot=(0,0,1;0rad)
  Width = 68
FEATURE [Part::Compound] Compound848
  Links = -> [Box673]
  Placement = pos=(0,0,-10) rot=(0,0,1;3.92699rad)
FEATURE [Part::Box] Box674  label="Krychle674"
  AttacherType = Attacher::AttachEngine3D
  Height = 10
  Length = 56
  Placement = pos=(-28,78,75) rot=(0,0,1;0rad)
  Width = 44
FEATURE [Part::Compound] Compound849
  Links = -> [Box674]
  Placement = pos=(0,0,-10) rot=(0,0,1;3.92699rad)
FEATURE [Part::Cut] Cut491
  Base = -> Compound848
  Tool = -> Compound849
FEATURE [Part::Box] Box675  label="Krychle675"
  AttacherType = Attacher::AttachEngine3D
  Height = 50
  Length = 42
  Placement = pos=(-21.0011,60.0051,31) rot=(0,0,1;0rad)
  Width = 62
FEATURE [Part::Compound] Compound850
  Links = -> [Box675]
  Placement = pos=(0,0,0) rot=(0,0,1;3.92699rad)
FEATURE [Part::Cut] Cut492
  Base = -> Cut491
  Tool = -> Compound850
FEATURE [Part::Cylinder] Cylinder1709  label="Válec1709"
  Angle = 360
  AttacherType = Attacher::AttachEngine3D
  Height = 40
  Placement = pos=(0,0,44) rot=(0,0,1;0rad)
  Radius = 74
FEATURE [Part::Cut] Cut493
  Base = -> Cut492
  Tool = -> Cylinder1709
FEATURE [Part::Cylinder] Cylinder1710  label="Válec1710"
  Angle = 360
  AttacherType = Attacher::AttachEngine3D
  Height = 50
  Placement = pos=(-24,140,72) rot=(1,0,0;1.5708rad)
  Radius = 1.5
FEATURE [Part::Cylinder] Cylinder1711  label="Válec1711"
  Angle = 360
  AttacherType = Attacher::AttachEngine3D
  Height = 50
  Placement = pos=(24,140,72) rot=(1,0,0;1.5708rad)
  Radius = 1.5
FEATURE [Part::Compound] Compound851
  Links = -> [Cylinder1710]
  Placement = pos=(0,0,0) rot=(0,0,1;3.92699rad)
FEATURE [Part::Compound] Compound852
  Links = -> [Cylinder1711]
  Placement = pos=(0,0,0) rot=(0,0,1;3.92699rad)
FEATURE [Part::Compound] Compound853
  Links = -> [Compound851,Compound852]
  Placement = pos=(0,0,-2) rot=(0,0,1;0rad)
FEATURE [Part::Cylinder] Cylinder1712  label="Válec1712"
  Angle = 360
  AttacherType = Attacher::AttachEngine3D
  Height = 3
  Placement = pos=(-24,128,72) rot=(1,0,0;1.5708rad)
  Radius = 3
FEATURE [Part::Compound] Compound854
  Links = -> [Cylinder1712]
  Placement = pos=(0,0,0) rot=(0,0,1;3.92699rad)
FEATURE [Part::Cylinder] Cylinder1713  label="Válec1713"
  Angle = 360
  AttacherType = Attacher::AttachEngine3D
  Height = 3
  Placement = pos=(24,128,72) rot=(1,0,0;1.5708rad)
  Radius = 3
FEATURE [Part::Compound] Compound855
  Links = -> [Cylinder1713]
  Placement = pos=(0,0,0) rot=(0,0,1;3.92699rad)
FEATURE [Part::Compound] Compound856
  Links = -> [Compound854,Compound855]
  Placement = pos=(0,0,-2) rot=(0,0,1;0rad)
FEATURE [Part::Chamfer] Chamfer052
  Base = -> Cut493
  Edges = 2 edges r=3: [Edge26,Edge37]
FEATURE [Part::Cut] Cut494
  Base = -> Chamfer052
  Tool = -> Compound856
FEATURE [Part::Cut] Cut495
  Base = -> Cut494
  Tool = -> Compound853
FEATURE [Part::Chamfer] Chamfer053
  Base = -> Cut490
  Edges = 2 edges r=3: [Edge2,Edge9]
FEATURE [Part::Box] Box680  label="Krychle680"
  AttacherType = Attacher::AttachEngine3D
  Height = 2
  Length = 6
  Placement = pos=(21,70,-48) rot=(0,0,1;0rad)
  Width = 6
FEATURE [Part::Box] Box681  label="Krychle681"
  AttacherType = Attacher::AttachEngine3D
  Height = 2
  Length = 7
  Placement = pos=(-28,70,-48) rot=(0,0,1;0rad)
  Width = 6
FEATURE [Part::Box] Box682  label="Krychle682"
  AttacherType = Attacher::AttachEngine3D
  Height = 2
  Length = 6
  Placement = pos=(-18,122,-48) rot=(0,0,1;0rad)
  Width = 6
FEATURE [Part::Box] Box683  label="Krychle683"
  AttacherType = Attacher::AttachEngine3D
  Height = 2
  Length = 6
  Placement = pos=(12,122,-48) rot=(0,0,1;0rad)
  Width = 6
FEATURE [Part::Compound] Compound859
  Links = -> [Box681,Box682,Box680,Box683]
  Placement = pos=(0,0,117) rot=(0,0,1;3.92699rad)
FEATURE [Part::Cylinder] Cylinder1718  label="Válec1718"
  Angle = 360
  AttacherType = Attacher::AttachEngine3D
  Height = 60
  Placement = pos=(-15,125,-80) rot=(0,0,1;0rad)
  Radius = 1.5
FEATURE [Part::Cylinder] Cylinder1719  label="Válec1719"
  Angle = 360
  AttacherType = Attacher::AttachEngine3D
  Height = 60
  Placement = pos=(15,125,-80) rot=(0,0,1;0rad)
  Radius = 1.5
FEATURE [Part::Cylinder] Cylinder1720  label="Válec1720"
  Angle = 360
  AttacherType = Attacher::AttachEngine3D
  Height = 60
  Placement = pos=(24,73,-80) rot=(0,0,1;0rad)
  Radius = 1.5
FEATURE [Part::Cylinder] Cylinder1721  label="Válec1721"
  Angle = 360
  AttacherType = Attacher::AttachEngine3D
  Height = 60
  Placement = pos=(-24,73,-80) rot=(0,0,1;0rad)
  Radius = 1.5
FEATURE [Part::Compound] Compound860
  Links = -> [Cylinder1720,Cylinder1721,Cylinder1718,Cylinder1719]
  Placement = pos=(0,0,100) rot=(0,0,1;3.92699rad)
FEATURE [Part::Cut] Cut496
  Base = -> Cut495
  Tool = -> Compound859
FEATURE [Part::Cut] Cut497
  Base = -> Cut496
  Tool = -> Compound860
FEATURE [Part::Box] Box684  label="Krychle684"
  AttacherType = Attacher::AttachEngine3D
  Height = 9
  Length = 66
  Placement = pos=(-33,60,75) rot=(0,0,1;0rad)
  Width = 14
FEATURE [Part::Compound] Compound861
  Links = -> [Box684]
  Placement = pos=(0,0,0) rot=(0,0,1;3.92699rad)
FEATURE [Part::Box] Box460  label="Krychle460"
  AttacherType = Attacher::AttachEngine3D
  Height = 2
  Length = 6
  Placement = pos=(-112,4,60) rot=(0,0,1;0rad)
  Width = 6
FEATURE [Part::Box] Box461  label="Krychle461"
  AttacherType = Attacher::AttachEngine3D
  Height = 20
  Length = 20
  Placement = pos=(-106,4,56) rot=(0,0,1;0rad)
  Width = 80
FEATURE [Part::Box] Box462  label="Krychle462"
  AttacherType = Attacher::AttachEngine3D
  Height = 2
  Length = 6
  Placement = pos=(-112,22,60) rot=(0,0,1;0rad)
  Width = 6
FEATURE [Part::Box] Box463  label="Krychle463"
  AttacherType = Attacher::AttachEngine3D
  Height = 2
  Length = 6
  Placement = pos=(-86,22,60) rot=(0,0,1;0rad)
  Width = 6
FEATURE [Part::Cylinder] Cylinder941  label="Válec941"
  Angle = 360
  AttacherType = Attacher::AttachEngine3D
  Height = 20
  Placement = pos=(-83,25,54) rot=(0,0,1;0rad)
  Radius = 1.5
FEATURE [Part::Box] Box464  label="Krychle464"
  AttacherType = Attacher::AttachEngine3D
  Height = 2
  Length = 6
  Placement = pos=(-86,4,60) rot=(0,0,1;0rad)
  Width = 6
FEATURE [Part::Compound] Compound510
  Links = -> [Box460,Box462,Box464,Box463]
FEATURE [Part::Cylinder] Cylinder942  label="Válec942"
  Angle = 360
  AttacherType = Attacher::AttachEngine3D
  Height = 20
  Placement = pos=(-83,7,54) rot=(0,0,1;0rad)
  Radius = 1.5
FEATURE [Part::Cylinder] Cylinder943  label="Válec943"
  Angle = 360
  AttacherType = Attacher::AttachEngine3D
  Height = 20
  Placement = pos=(-109,7,54) rot=(0,0,1;0rad)
  Radius = 1.5
FEATURE [Part::Cylinder] Cylinder944  label="Válec944"
  Angle = 360
  AttacherType = Attacher::AttachEngine3D
  Height = 20
  Placement = pos=(-109,25,54) rot=(0,0,1;0rad)
  Radius = 1.5
FEATURE [Part::Compound] Compound511
  Links = -> [Cylinder942,Cylinder941,Cylinder943,Cylinder944]
FEATURE [Part::Box] Box465  label="Krychle465"
  AttacherType = Attacher::AttachEngine3D
  Height = 26
  Length = 38
  Placement = pos=(-112,0,56) rot=(0,0,1;0rad)
  Width = 32
FEATURE [Part::Cylinder] Cylinder945  label="Válec945"
  Angle = 360
  AttacherType = Attacher::AttachEngine3D
  Height = 3
  Placement = pos=(-112,16,66) rot=(0,1,0;1.5708rad)
  Radius = 5
FEATURE [Part::Cylinder] Cylinder946  label="Válec946"
  Angle = 360
  AttacherType = Attacher::AttachEngine3D
  Height = 20
  Placement = pos=(-117,16,66) rot=(0,1,0;1.5708rad)
  Radius = 2.5
FEATURE [Part::Box] Box466  label="Krychle466"
  AttacherType = Attacher::AttachEngine3D
  Height = 6
  Length = 51
  Placement = pos=(-112,-24,76) rot=(0,0,1;0rad)
  Width = 24
FEATURE [Part::Cylinder] Cylinder947  label="Válec947"
  Angle = 360
  AttacherType = Attacher::AttachEngine3D
  Height = 10
  Placement = pos=(0,0,72) rot=(0,0,1;0rad)
  Radius = 74
FEATURE [Part::Cylinder] Cylinder948  label="Válec948"
  Angle = 360
  AttacherType = Attacher::AttachEngine3D
  Height = 32
  Placement = pos=(0,0,50) rot=(0,0,1;0rad)
  Radius = 74
FEATURE [Part::Box] Box467  label="Krychle467"
  AttacherType = Attacher::AttachEngine3D
  Height = 26
  Length = 50
  Placement = pos=(-112,-24,56) rot=(0,0,1;0rad)
  Width = 6
FEATURE [Part::Cylinder] Cylinder949  label="Válec949"
  Angle = 360
  AttacherType = Attacher::AttachEngine3D
  Height = 20
  Placement = pos=(-86,-10,66) rot=(0,0,1;0rad)
  Radius = 2.5
FEATURE [Part::Cylinder] Cylinder950  label="Válec950"
  Angle = 360
  AttacherType = Attacher::AttachEngine3D
  Height = 20
  Placement = pos=(-102,-10,66) rot=(0,0,1;0rad)
  Radius = 2.5
FEATURE [Part::Compound] Compound513
  Links = -> [Cylinder950,Cylinder949]
FEATURE [Part::Cut] Cut430
  Base = -> Box467
  Tool = -> Cylinder948
FEATURE [Part::Chamfer] Chamfer006
  Base = -> Cut430
  Edges = 1 edges r=20: [Edge4]
FEATURE [Part::Cut] Cut432
  Base = -> Box466
  Tool = -> Cylinder947
FEATURE [Part::Cut] Cut431
  Base = -> Cut432
  Tool = -> Compound513
FEATURE [Part::Cut] Cut433
  Base = -> Box465
  Tool = -> Box461
FEATURE [Part::Cut] Cut434
  Base = -> Cut433
  Tool = -> Compound510
FEATURE [Part::Cut] Cut427
  Base = -> Cut434
  Tool = -> Compound511
FEATURE [Part::Cut] Cut428
  Base = -> Cut427
  Tool = -> Cylinder946
FEATURE [Part::Cut] Cut429
  Base = -> Cut428
  Tool = -> Cylinder945
FEATURE [Part::Chamfer] Chamfer007
  Base = -> Cut429
  Edges = 1 edges r=2: [Edge4]
FEATURE [Part::Compound] Compound512  label="stabilo_holdo_left002"
  Links = -> [Chamfer006,Cut431,Chamfer007]
FEATURE [Part::Mirroring] mirror002  label="stabilo_holdo_right001"
  Base = (0,0,0)
  Normal = (1,0,0)
  Source = -> Compound512
FEATURE [Part::Box] Box685  label="Krychle685"
  AttacherType = Attacher::AttachEngine3D
  Height = 18
  Length = 42
  Placement = pos=(-21,-23,22) rot=(0,0,1;0rad)
  Width = 8
FEATURE [Part::Compound] Compound862
  Links = -> [Box685]
  Placement = pos=(63.64,-63.64,43) rot=(0,0,1;3.92699rad)
FEATURE [Part::Cylinder] Cylinder1722  label="Válec1722"
  Angle = 360
  AttacherType = Attacher::AttachEngine3D
  Height = 50
  Placement = pos=(-18,100,72) rot=(1,0,0;1.5708rad)
  Radius = 1.5
FEATURE [Part::Compound] Compound863
  Links = -> [Cylinder1722]
  Placement = pos=(0,0,0) rot=(0,0,1;3.92699rad)
FEATURE [Part::Cylinder] Cylinder1723  label="Válec1723"
  Angle = 360
  AttacherType = Attacher::AttachEngine3D
  Height = 50
  Placement = pos=(18,100,72) rot=(1,0,0;1.5708rad)
  Radius = 1.5
FEATURE [Part::Compound] Compound864
  Links = -> [Cylinder1723]
  Placement = pos=(0,0,0) rot=(0,0,1;3.92699rad)
FEATURE [Part::Compound] Compound865
  Links = -> [Compound863,Compound864]
  Placement = pos=(0,0,1) rot=(0,0,1;0rad)
FEATURE [Part::Cylinder] Cylinder1724  label="Válec1724"
  Angle = 360
  AttacherType = Attacher::AttachEngine3D
  Height = 40
  Placement = pos=(0,0,44) rot=(0,0,1;0rad)
  Radius = 74
FEATURE [Part::Cut] Cut498
  Base = -> Compound862
  Tool = -> Cylinder1724
FEATURE [Part::Box] Box686  label="Krychle686"
  AttacherType = Attacher::AttachEngine3D
  Height = 6
  Length = 6
  Placement = pos=(15,64,-50) rot=(0,0,1;0rad)
  Width = 4
FEATURE [Part::Box] Box687  label="Krychle687"
  AttacherType = Attacher::AttachEngine3D
  Height = 6
  Length = 6
  Placement = pos=(-21,64,-50) rot=(0,0,1;0rad)
  Width = 4
FEATURE [Part::Compound] Compound866
  Links = -> [Box687,Box686]
  Placement = pos=(0,0,120) rot=(0,0,1;3.92699rad)
FEATURE [Part::Cylinder] Cylinder1725  label="Válec1725"
  Angle = 360
  AttacherType = Attacher::AttachEngine3D
  Height = 50
  Placement = pos=(-18,100,72) rot=(1,0,0;1.5708rad)
  Radius = 1.5
FEATURE [Part::Compound] Compound869
  Links = -> [Cylinder1725]
  Placement = pos=(0,0,0) rot=(0,0,1;3.92699rad)
FEATURE [Part::Cylinder] Cylinder1726  label="Válec1726"
  Angle = 360
  AttacherType = Attacher::AttachEngine3D
  Height = 50
  Placement = pos=(18,100,72) rot=(1,0,0;1.5708rad)
  Radius = 1.5
FEATURE [Part::Compound] Compound868
  Links = -> [Cylinder1726]
  Placement = pos=(0,0,0) rot=(0,0,1;3.92699rad)
FEATURE [Part::Compound] Compound867
  Links = -> [Compound869,Compound868]
  Placement = pos=(0,0,1) rot=(0,0,1;0rad)
FEATURE [Part::Cut] Cut499
  Base = -> Cut498
  Tool = -> Compound867
FEATURE [Part::Cut] Cut500
  Base = -> Cut468
  Tool = -> Compound865
FEATURE [Part::Cut] Cut501
  Base = -> Cut500
  Tool = -> Compound866
FEATURE [Part::Compound] Compound870  label="Base_encoder-lowhold"
  Links = -> [Cut497,Chamfer053,Cut499]
FEATURE [Part::Cylinder] Cylinder1727  label="Válec1727"
  Angle = 360
  AttacherType = Attacher::AttachEngine3D
  Height = 3
  Placement = pos=(-15,125,-80) rot=(0,0,1;0rad)
  Radius = 3
FEATURE [Part::Cylinder] Cylinder1728  label="Válec1728"
  Angle = 360
  AttacherType = Attacher::AttachEngine3D
  Height = 3
  Placement = pos=(15,125,-80) rot=(0,0,1;0rad)
  Radius = 3
FEATURE [Part::Cylinder] Cylinder1729  label="Válec1729"
  Angle = 360
  AttacherType = Attacher::AttachEngine3D
  Height = 3
  Placement = pos=(24,73,-80) rot=(0,0,1;0rad)
  Radius = 3
FEATURE [Part::Cylinder] Cylinder1730  label="Válec1730"
  Angle = 360
  AttacherType = Attacher::AttachEngine3D
  Height = 3
  Placement = pos=(-24,73,-80) rot=(0,0,1;0rad)
  Radius = 3
FEATURE [Part::Compound] Compound871
  Links = -> [Cylinder1729,Cylinder1730,Cylinder1727,Cylinder1728]
  Placement = pos=(0,0,135) rot=(0,0,1;3.92699rad)
FEATURE [Part::Box] Box688  label="Krychle688"
  AttacherType = Attacher::AttachEngine3D
  Height = 50
  Length = 42
  Placement = pos=(-21.0011,60.0051,31) rot=(0,0,1;0rad)
  Width = 62
FEATURE [Part::Compound] Compound872
  Links = -> [Box688]
  Placement = pos=(0,0,0) rot=(0,0,1;3.92699rad)
FEATURE [Part::Box] Box689  label="Krychle689"
  AttacherType = Attacher::AttachEngine3D
  Height = 10
  Length = 54
  Placement = pos=(-27.0044,59.998,75) rot=(0,0,1;0rad)
  Width = 68
FEATURE [Part::Compound] Compound873
  Links = -> [Box689]
  Placement = pos=(0,0,-20) rot=(0,0,1;3.92699rad)
FEATURE [Part::Cut] Cut502
  Base = -> Compound873
  Tool = -> Compound872
FEATURE [Part::Cylinder] Cylinder1731  label="Válec1731"
  Angle = 360
  AttacherType = Attacher::AttachEngine3D
  Height = 60
  Placement = pos=(-15,125,-80) rot=(0,0,1;0rad)
  Radius = 1.5
FEATURE [Part::Cylinder] Cylinder1732  label="Válec1732"
  Angle = 360
  AttacherType = Attacher::AttachEngine3D
  Height = 60
  Placement = pos=(15,125,-80) rot=(0,0,1;0rad)
  Radius = 1.5
FEATURE [Part::Cylinder] Cylinder1733  label="Válec1733"
  Angle = 360
  AttacherType = Attacher::AttachEngine3D
  Height = 60
  Placement = pos=(24,73,-80) rot=(0,0,1;0rad)
  Radius = 1.5
FEATURE [Part::Cylinder] Cylinder1734  label="Válec1734"
  Angle = 360
  AttacherType = Attacher::AttachEngine3D
  Height = 60
  Placement = pos=(-24,73,-80) rot=(0,0,1;0rad)
  Radius = 1.5
FEATURE [Part::Compound] Compound874
  Links = -> [Cylinder1733,Cylinder1734,Cylinder1731,Cylinder1732]
  Placement = pos=(0,0,100) rot=(0,0,1;3.92699rad)
FEATURE [Part::Cylinder] Cylinder1735  label="Válec1735"
  Angle = 360
  AttacherType = Attacher::AttachEngine3D
  Height = 40
  Placement = pos=(0,0,44) rot=(0,0,1;0rad)
  Radius = 74
FEATURE [Part::Compound] Compound875  label="encoder-pulley"
  Links = -> [Cylinder1641,Cylinder1642]
FEATURE [Part::Box] Box690  label="Krychle690"
  AttacherType = Attacher::AttachEngine3D
  Height = 10
  Length = 42
  Placement = pos=(-21,-23,22) rot=(0,0,1;0rad)
  Width = 8
FEATURE [Part::Cylinder] Cylinder1736  label="Válec1736"
  Angle = 360
  AttacherType = Attacher::AttachEngine3D
  Height = 40
  Placement = pos=(0,0,44) rot=(0,0,1;0rad)
  Radius = 74
FEATURE [Part::Compound] Compound876
  Links = -> [Box690]
  Placement = pos=(63.64,-63.64,43) rot=(0,0,1;3.92699rad)
FEATURE [Part::Cut] Cut506
  Base = -> Compound876
  Placement = pos=(0,0,-10) rot=(0,0,1;0rad)
  Tool = -> Cylinder1736
FEATURE [Part::Cylinder] Cylinder1737  label="Válec1737"
  Angle = 360
  AttacherType = Attacher::AttachEngine3D
  Height = 50
  Placement = pos=(-9,100,59) rot=(1,0,0;1.5708rad)
  Radius = 1.5
FEATURE [Part::Cylinder] Cylinder1738  label="Válec1738"
  Angle = 360
  AttacherType = Attacher::AttachEngine3D
  Height = 50
  Placement = pos=(9,100,59) rot=(1,0,0;1.5708rad)
  Radius = 1.5
FEATURE [Part::Compound] Compound878
  Links = -> [Cylinder1738]
  Placement = pos=(0,0,0) rot=(0,0,1;3.92699rad)
FEATURE [Part::Compound] Compound879
  Links = -> [Cylinder1737]
  Placement = pos=(0,0,0) rot=(0,0,1;3.92699rad)
FEATURE [Part::Compound] Compound877
  Links = -> [Compound879,Compound878]
  Placement = pos=(0,0,1) rot=(0,0,1;0rad)
FEATURE [Part::Box] Box691  label="Krychle691"
  AttacherType = Attacher::AttachEngine3D
  Height = 6
  Length = 6
  Placement = pos=(6,66,-63) rot=(0,0,1;0rad)
  Width = 4
FEATURE [Part::Box] Box692  label="Krychle692"
  AttacherType = Attacher::AttachEngine3D
  Height = 6
  Length = 6
  Placement = pos=(-12,66,-63) rot=(0,0,1;0rad)
  Width = 4
FEATURE [Part::Compound] Compound880
  Links = -> [Box692,Box691]
  Placement = pos=(0,0,120) rot=(0,0,1;3.92699rad)
FEATURE [Part::Cylinder] Cylinder1739  label="Válec1739"
  Angle = 360
  AttacherType = Attacher::AttachEngine3D
  Height = 50
  Placement = pos=(9,100,59) rot=(1,0,0;1.5708rad)
  Radius = 1.5
FEATURE [Part::Cylinder] Cylinder1740  label="Válec1740"
  Angle = 360
  AttacherType = Attacher::AttachEngine3D
  Height = 50
  Placement = pos=(-9,100,59) rot=(1,0,0;1.5708rad)
  Radius = 1.5
FEATURE [Part::Compound] Compound881
  Links = -> [Cylinder1739]
  Placement = pos=(0,0,0) rot=(0,0,1;3.92699rad)
FEATURE [Part::Compound] Compound882
  Links = -> [Cylinder1740]
  Placement = pos=(0,0,0) rot=(0,0,1;3.92699rad)
FEATURE [Part::Compound] Compound883
  Links = -> [Compound882,Compound881]
  Placement = pos=(0,0,1) rot=(0,0,1;0rad)
FEATURE [Part::Cut] Cut507
  Base = -> Cut506
  Tool = -> Compound883
FEATURE [Part::Cut] Cut508
  Base = -> Cut501
  Tool = -> Compound877
FEATURE [Part::Cut] Cut509
  Base = -> Cut508
  Tool = -> Compound880
FEATURE [Part::Cut] Cut510
  Base = -> Cut502
  Tool = -> Cylinder1735
FEATURE [Part::Chamfer] Chamfer054
  Base = -> Cut510
  Edges = 2 edges r=3: [Edge2,Edge13]
FEATURE [Part::Chamfer] Chamfer055
  Base = -> Chamfer054
  Edges = 2 edges r=2: [Edge3,Edge22]
FEATURE [Part::Chamfer] Chamfer056
  Base = -> Chamfer055
  Edges = 1 edges r=1: [Edge27]
FEATURE [Part::Cut] Cut511
  Base = -> Chamfer056
  Tool = -> Compound874
FEATURE [Part::Cut] Cut512
  Base = -> Cut511
  Tool = -> Compound871
FEATURE [Part::Compound] Compound884  label="Base_encoder-tophold"
  Links = -> [Cut507,Cut512]
FEATURE [Part::Box] Box693  label="Krychle693"
  AttacherType = Attacher::AttachEngine3D
  Height = 60
  Length = 200
  Placement = pos=(0,0,-5) rot=(0,0,-1;0.383972rad)
  Width = 200
FEATURE [Part::Box] Box694  label="Krychle694"
  AttacherType = Attacher::AttachEngine3D
  Height = 12
  Length = 200
  Placement = pos=(70.7107,70.7107,-5) rot=(0,0,1;3.92699rad)
  Width = 120
FEATURE [Part::Box] Box695  label="Krychle695"
  AttacherType = Attacher::AttachEngine3D
  Height = 60
  Length = 200
  Placement = pos=(0,0,-5) rot=(0,0,1;3.52556rad)
  Width = 200
FEATURE [Part::Cut] Cut513
  Base = -> Box694
  Tool = -> Box693
FEATURE [Part::Cut] Cut514
  Base = -> Cut513
  Placement = pos=(0,0,34) rot=(0,0,1;0rad)
  Tool = -> Box695
FEATURE [Part::FeaturePython] Tube038  # WARN: FeaturePython — macro-defined, semantics opaque (R4)
  AttacherType = Attacher::AttachEngine3D
  Height = 55
  InnerRadius = 68
  OuterRadius = 74
  Placement = pos=(0,0,29) rot=(0,0,1;0rad)
FEATURE [Part::Box] Box696  label="Krychle696"
  AttacherType = Attacher::AttachEngine3D
  Height = 60
  Length = 200
  Placement = pos=(0,0,-5) rot=(0,0,-1;0.680678rad)
  Width = 200
FEATURE [Part::Box] Box697  label="Krychle697"
  AttacherType = Attacher::AttachEngine3D
  Height = 60
  Length = 200
  Placement = pos=(0,0,-5) rot=(0,0,1;3.82227rad)
  Width = 200
FEATURE [Part::Box] Box698  label="Krychle698"
  AttacherType = Attacher::AttachEngine3D
  Height = 14
  Length = 200
  Placement = pos=(70.7107,70.7107,-5) rot=(0,0,1;3.92699rad)
  Width = 120
FEATURE [Part::Cut] Cut515
  Base = -> Box698
  Tool = -> Box696
FEATURE [Part::Cut] Cut516
  Base = -> Cut515
  Placement = pos=(0,0,46) rot=(0,0,1;0rad)
  Tool = -> Box697
FEATURE [Part::Common] Common
  Base = -> Cut514
  Tool = -> Tube038
FEATURE [Part::FeaturePython] Tube039  # WARN: FeaturePython — macro-defined, semantics opaque (R4)
  AttacherType = Attacher::AttachEngine3D
  Height = 55
  InnerRadius = 68
  OuterRadius = 74
  Placement = pos=(0,0,29) rot=(0,0,1;0rad)
FEATURE [Part::Common] Common001
  Base = -> Cut516
  Tool = -> Tube039
FEATURE [Part::Compound] Compound885
  Links = -> [Common,Common001]
FEATURE [Part::Cylinder] Cylinder1741  label="Válec1741"
  Angle = 360
  AttacherType = Attacher::AttachEngine3D
  Height = 72
  Placement = pos=(71,-1.8e-14,0) rot=(0,0,1;1.5708rad)
  Radius = 1.5
FEATURE [Part::Cylinder] Cylinder1742  label="Válec1742"
  Angle = 360
  AttacherType = Attacher::AttachEngine3D
  Height = 72
  Placement = pos=(35.5,61.4878,0) rot=(0,0,1;2.61799rad)
  Radius = 1.5
FEATURE [Part::Cylinder] Cylinder1743  label="Válec1743"
  Angle = 360
  AttacherType = Attacher::AttachEngine3D
  Height = 72
  Placement = pos=(61.4878,-35.5,0) rot=(0,0,1;1.0472rad)
  Radius = 1.5
FEATURE [Part::Cylinder] Cylinder1744  label="Válec1744"
  Angle = 360
  AttacherType = Attacher::AttachEngine3D
  Height = 72
  Placement = pos=(35.5,-61.4878,0) rot=(0,0,1;0.523599rad)
  Radius = 1.5
FEATURE [Part::Cylinder] Cylinder1745  label="Válec1745"
  Angle = 360
  AttacherType = Attacher::AttachEngine3D
  Height = 72
  Placement = pos=(-35.5,-61.4878,0) rot=(0,0,-1;0.523599rad)
  Radius = 1.5
FEATURE [Part::Cylinder] Cylinder1746  label="Válec1746"
  Angle = 360
  AttacherType = Attacher::AttachEngine3D
  Height = 72
  Placement = pos=(-71,2.7e-14,0) rot=(0,0,-1;1.5708rad)
  Radius = 1.5
FEATURE [Part::Cylinder] Cylinder1747  label="Válec1747"
  Angle = 360
  AttacherType = Attacher::AttachEngine3D
  Height = 72
  Placement = pos=(-61.4878,-35.5,0) rot=(0,0,-1;1.0472rad)
  Radius = 1.5
FEATURE [Part::Cylinder] Cylinder1748  label="Válec1748"
  Angle = 360
  AttacherType = Attacher::AttachEngine3D
  Height = 72
  Placement = pos=(61.4878,35.5,0) rot=(0,0,1;2.0944rad)
  Radius = 1.5
FEATURE [Part::Cylinder] Cylinder1749  label="Válec1749"
  Angle = 360
  AttacherType = Attacher::AttachEngine3D
  Height = 72
  Placement = pos=(0,-71,0) rot=(0,0,1;0rad)
  Radius = 1.5
FEATURE [Part::Cylinder] Cylinder1750  label="Válec1750"
  Angle = 360
  AttacherType = Attacher::AttachEngine3D
  Height = 72
  Placement = pos=(-35.5,61.4878,0) rot=(0,0,1;3.66519rad)
  Radius = 1.5
FEATURE [Part::Cylinder] Cylinder1751  label="Válec1751"
  Angle = 360
  AttacherType = Attacher::AttachEngine3D
  Height = 72
  Placement = pos=(-61.4878,35.5,0) rot=(0,0,1;4.18879rad)
  Radius = 1.5
FEATURE [Part::Cylinder] Cylinder1752  label="Válec1752"
  Angle = 360
  AttacherType = Attacher::AttachEngine3D
  Height = 72
  Placement = pos=(3.1e-14,71,0) rot=(0,0,1;3.14159rad)
  Radius = 1.5
FEATURE [Part::Compound] Compound886
  Links = -> [Cylinder1749,Cylinder1744,Cylinder1743,Cylinder1741,Cylinder1748,Cylinder1742,Cylinder1752,Cylinder1750,Cylinder1751,Cylinder1746,Cylinder1747,Cylinder1745]
FEATURE [Part::Cut] Cut517  label="Base_pulley-cover"
  Base = -> Compound885
  Tool = -> Compound886
FEATURE [Part::Box] Box482  label="Krychle482"
  AttacherType = Attacher::AttachEngine3D
  Height = 55
  Length = 148
  Placement = pos=(-74,0,29) rot=(0,0,1;0rad)
  Width = 74
FEATURE [Part::Cylinder] Cylinder972  label="Válec972"
  Angle = 360
  AttacherType = Attacher::AttachEngine3D
  Height = 51
  Placement = pos=(0,0,29) rot=(0,0,1;0rad)
  Radius = 74
FEATURE [Part::Box] Box484  label="Krychle484"
  AttacherType = Attacher::AttachEngine3D
  Height = 55
  Length = 148
  Placement = pos=(-74,48,29) rot=(0,0,1;0rad)
  Width = 26
FEATURE [Part::Cut] Cut451
  Base = -> Box482
  Tool = -> Cylinder972
FEATURE [Part::Cut] Cut452
  Base = -> Cut451
  Tool = -> Box484
FEATURE [Part::Cylinder] Cylinder1753  label="Válec1753"
  Angle = 360
  AttacherType = Attacher::AttachEngine3D
  Height = 50
  Placement = pos=(-71,80,73) rot=(1,0,0;1.5708rad)
  Radius = 1.5
FEATURE [Part::Cylinder] Cylinder1754  label="Válec1754"
  Angle = 360
  AttacherType = Attacher::AttachEngine3D
  Height = 50
  Placement = pos=(71,80,39) rot=(1,0,0;1.5708rad)
  Radius = 1.5
FEATURE [Part::Cylinder] Cylinder1755  label="Válec1755"
  Angle = 360
  AttacherType = Attacher::AttachEngine3D
  Height = 50
  Placement = pos=(-71,80,39) rot=(1,0,0;1.5708rad)
  Radius = 1.5
FEATURE [Part::Cylinder] Cylinder1756  label="Válec1756"
  Angle = 360
  AttacherType = Attacher::AttachEngine3D
  Height = 50
  Placement = pos=(71,80,73) rot=(1,0,0;1.5708rad)
  Radius = 1.5
FEATURE [Part::Cylinder] Cylinder1757  label="Válec1757"
  Angle = 360
  AttacherType = Attacher::AttachEngine3D
  Height = 50
  Placement = pos=(-71,80,56) rot=(1,0,0;1.5708rad)
  Radius = 1.5
FEATURE [Part::Cylinder] Cylinder1758  label="Válec1758"
  Angle = 360
  AttacherType = Attacher::AttachEngine3D
  Height = 50
  Placement = pos=(71,80,56) rot=(1,0,0;1.5708rad)
  Radius = 1.5
FEATURE [Part::Compound] Compound887
  Links = -> [Cylinder1753,Cylinder1754,Cylinder1755,Cylinder1756,Cylinder1757,Cylinder1758]
FEATURE [Part::Box] Box512  label="Krychle512"
  AttacherType = Attacher::AttachEngine3D
  Height = 6
  Length = 8
  Placement = pos=(-75,38,36) rot=(0,0,1;0rad)
  Width = 2
FEATURE [Part::Box] Box513  label="Krychle513"
  AttacherType = Attacher::AttachEngine3D
  Height = 6
  Length = 8
  Placement = pos=(67,38,36) rot=(0,0,1;0rad)
  Width = 2
FEATURE [Part::Box] Box514  label="Krychle514"
  AttacherType = Attacher::AttachEngine3D
  Height = 6
  Length = 8
  Placement = pos=(67,38,70) rot=(0,0,1;0rad)
  Width = 2
FEATURE [Part::Box] Box515  label="Krychle515"
  AttacherType = Attacher::AttachEngine3D
  Height = 6
  Length = 8
  Placement = pos=(-75,38,70) rot=(0,0,1;0rad)
  Width = 2
FEATURE [Part::Box] Box516  label="Krychle516"
  AttacherType = Attacher::AttachEngine3D
  Height = 6
  Length = 8
  Placement = pos=(-75,38,53) rot=(0,0,1;0rad)
  Width = 2
FEATURE [Part::Box] Box517  label="Krychle517"
  AttacherType = Attacher::AttachEngine3D
  Height = 6
  Length = 8
  Placement = pos=(67,38,53) rot=(0,0,1;0rad)
  Width = 2
FEATURE [Part::Compound] Compound530
  Links = -> [Box512,Box513,Box514,Box515,Box516,Box517]
FEATURE [Part::Cut] Cut518
  Base = -> Cut452
  Tool = -> Compound887
FEATURE [Part::Cut] Cut519
  Base = -> Cut518
  Tool = -> Compound530
FEATURE [Part::Box] Box699  label="Krychle699"
  AttacherType = Attacher::AttachEngine3D
  Height = 2
  Length = 6
  Placement = pos=(-3,-75,39) rot=(0,0,1;0rad)
  Width = 8
FEATURE [Part::Box] Box700  label="Krychle700"
  AttacherType = Attacher::AttachEngine3D
  Height = 2
  Length = 6
  Placement = pos=(34.9019,-66.4519,39) rot=(0,0,1;0.523599rad)
  Width = 8
FEATURE [Part::Box] Box701  label="Krychle701"
  AttacherType = Attacher::AttachEngine3D
  Height = 2
  Length = 6
  Placement = pos=(63.4519,-40.0981,39) rot=(0,0,1;1.0472rad)
  Width = 8
FEATURE [Part::Box] Box702  label="Krychle702"
  AttacherType = Attacher::AttachEngine3D
  Height = 2
  Length = 6
  Placement = pos=(75,-3,39) rot=(0,0,1;1.5708rad)
  Width = 8
FEATURE [Part::Box] Box703  label="Krychle703"
  AttacherType = Attacher::AttachEngine3D
  Height = 2
  Length = 6
  Placement = pos=(66.4519,34.9019,39) rot=(0,0,1;2.0944rad)
  Width = 8
FEATURE [Part::Box] Box704  label="Krychle704"
  AttacherType = Attacher::AttachEngine3D
  Height = 2
  Length = 6
  Placement = pos=(40.0981,63.4519,39) rot=(0,0,1;2.61799rad)
  Width = 8
FEATURE [Part::Box] Box705  label="Krychle705"
  AttacherType = Attacher::AttachEngine3D
  Height = 2
  Length = 6
  Placement = pos=(3,75,39) rot=(0,0,1;3.14159rad)
  Width = 8
FEATURE [Part::Box] Box706  label="Krychle706"
  AttacherType = Attacher::AttachEngine3D
  Height = 2
  Length = 6
  Placement = pos=(-34.9019,66.4519,39) rot=(0,0,1;3.66519rad)
  Width = 8
FEATURE [Part::Box] Box707  label="Krychle707"
  AttacherType = Attacher::AttachEngine3D
  Height = 2
  Length = 6
  Placement = pos=(-63.4519,40.0981,39) rot=(0,0,1;4.18879rad)
  Width = 8
FEATURE [Part::Box] Box708  label="Krychle708"
  AttacherType = Attacher::AttachEngine3D
  Height = 2
  Length = 6
  Placement = pos=(-75,3,39) rot=(0,0,-1;1.5708rad)
  Width = 8
FEATURE [Part::Box] Box709  label="Krychle709"
  AttacherType = Attacher::AttachEngine3D
  Height = 2
  Length = 6
  Placement = pos=(-66.4519,-34.9019,39) rot=(0,0,-1;1.0472rad)
  Width = 8
FEATURE [Part::Box] Box710  label="Krychle710"
  AttacherType = Attacher::AttachEngine3D
  Height = 2
  Length = 6
  Placement = pos=(-40.0981,-63.4519,39) rot=(0,0,-1;0.523599rad)
  Width = 8
FEATURE [Part::Compound] Compound888
  Links = -> [Box699,Box700,Box701,Box702,Box703,Box704,Box705,Box706,Box707,Box708,Box709,Box710]
FEATURE [Part::Cut] Cut520
  Base = -> Cut519
  Tool = -> Compound888
FEATURE [Part::Box] Box425  label="Krychle425"
  AttacherType = Attacher::AttachEngine3D
  Height = 2
  Length = 6
  Placement = pos=(-112,4,60) rot=(0,0,1;0rad)
  Width = 6
FEATURE [Part::Box] Box426  label="Krychle426"
  AttacherType = Attacher::AttachEngine3D
  Height = 20
  Length = 20
  Placement = pos=(-106,4,56) rot=(0,0,1;0rad)
  Width = 80
FEATURE [Part::Box] Box427  label="Krychle427"
  AttacherType = Attacher::AttachEngine3D
  Height = 2
  Length = 6
  Placement = pos=(-112,22,60) rot=(0,0,1;0rad)
  Width = 6
FEATURE [Part::Box] Box428  label="Krychle428"
  AttacherType = Attacher::AttachEngine3D
  Height = 2
  Length = 6
  Placement = pos=(-86,22,60) rot=(0,0,1;0rad)
  Width = 6
FEATURE [Part::Cylinder] Cylinder899  label="Válec899"
  Angle = 360
  AttacherType = Attacher::AttachEngine3D
  Height = 20
  Placement = pos=(-83,25,54) rot=(0,0,1;0rad)
  Radius = 1.5
FEATURE [Part::Box] Box429  label="Krychle429"
  AttacherType = Attacher::AttachEngine3D
  Height = 2
  Length = 6
  Placement = pos=(-86,4,60) rot=(0,0,1;0rad)
  Width = 6
FEATURE [Part::Compound] Compound495
  Links = -> [Box425,Box427,Box429,Box428]
FEATURE [Part::Cylinder] Cylinder900  label="Válec900"
  Angle = 360
  AttacherType = Attacher::AttachEngine3D
  Height = 20
  Placement = pos=(-83,7,54) rot=(0,0,1;0rad)
  Radius = 1.5
FEATURE [Part::Cylinder] Cylinder901  label="Válec901"
  Angle = 360
  AttacherType = Attacher::AttachEngine3D
  Height = 20
  Placement = pos=(-109,7,54) rot=(0,0,1;0rad)
  Radius = 1.5
FEATURE [Part::Cylinder] Cylinder902  label="Válec902"
  Angle = 360
  AttacherType = Attacher::AttachEngine3D
  Height = 20
  Placement = pos=(-109,25,54) rot=(0,0,1;0rad)
  Radius = 1.5
FEATURE [Part::Compound] Compound496
  Links = -> [Cylinder900,Cylinder899,Cylinder901,Cylinder902]
FEATURE [Part::Box] Box430  label="Krychle430"
  AttacherType = Attacher::AttachEngine3D
  Height = 26
  Length = 38
  Placement = pos=(-112,0,56) rot=(0,0,1;0rad)
  Width = 32
FEATURE [Part::Cylinder] Cylinder903  label="Válec903"
  Angle = 360
  AttacherType = Attacher::AttachEngine3D
  Height = 3
  Placement = pos=(-112,16,66) rot=(0,1,0;1.5708rad)
  Radius = 5
FEATURE [Part::Cylinder] Cylinder904  label="Válec904"
  Angle = 360
  AttacherType = Attacher::AttachEngine3D
  Height = 20
  Placement = pos=(-117,16,66) rot=(0,1,0;1.5708rad)
  Radius = 2.5
FEATURE [Part::Box] Box431  label="Krychle431"
  AttacherType = Attacher::AttachEngine3D
  Height = 6
  Length = 51
  Placement = pos=(-112,-24,76) rot=(0,0,1;0rad)
  Width = 24
FEATURE [Part::Cylinder] Cylinder905  label="Válec905"
  Angle = 360
  AttacherType = Attacher::AttachEngine3D
  Height = 10
  Placement = pos=(0,0,72) rot=(0,0,1;0rad)
  Radius = 74
FEATURE [Part::Cylinder] Cylinder906  label="Válec906"
  Angle = 360
  AttacherType = Attacher::AttachEngine3D
  Height = 32
  Placement = pos=(0,0,50) rot=(0,0,1;0rad)
  Radius = 74
FEATURE [Part::Box] Box432  label="Krychle432"
  AttacherType = Attacher::AttachEngine3D
  Height = 26
  Length = 50
  Placement = pos=(-112,-24,56) rot=(0,0,1;0rad)
  Width = 6
FEATURE [Part::Cylinder] Cylinder907  label="Válec907"
  Angle = 360
  AttacherType = Attacher::AttachEngine3D
  Height = 20
  Placement = pos=(-86,-10,66) rot=(0,0,1;0rad)
  Radius = 2.5
FEATURE [Part::Cylinder] Cylinder908  label="Válec908"
  Angle = 360
  AttacherType = Attacher::AttachEngine3D
  Height = 20
  Placement = pos=(-102,-10,66) rot=(0,0,1;0rad)
  Radius = 2.5
FEATURE [Part::Cut] Cut406
  Base = -> Box432
  Tool = -> Cylinder906
FEATURE [Part::Chamfer] Chamfer003
  Base = -> Cut406
  Edges = 1 edges r=20: [Edge4]
FEATURE [Part::Cut] Cut408
  Base = -> Box431
  Tool = -> Cylinder905
FEATURE [Part::Cut] Cut409
  Base = -> Box430
  Tool = -> Box426
FEATURE [Part::Cut] Cut410
  Base = -> Cut409
  Tool = -> Compound495
FEATURE [Part::Cut] Cut403
  Base = -> Cut410
  Tool = -> Compound496
FEATURE [Part::Cut] Cut404
  Base = -> Cut403
  Tool = -> Cylinder904
FEATURE [Part::Cut] Cut405
  Base = -> Cut404
  Tool = -> Cylinder903
FEATURE [Part::Chamfer] Chamfer004
  Base = -> Cut405
  Edges = 1 edges r=2: [Edge4]
FEATURE [Part::Compound] Compound498
  Links = -> [Cylinder908,Cylinder907]
FEATURE [Part::Cut] Cut407
  Base = -> Cut408
  Tool = -> Compound498
FEATURE [Part::Compound] Compound497  label="stabilo_holdo_left"
  Links = -> [Chamfer003,Cut407,Chamfer004]
  Placement = pos=(0,0,2) rot=(0,0,1;0rad)
FEATURE [Part::Box] Box521  label="Krychle521"
  AttacherType = Attacher::AttachEngine3D
  Height = 14
  Length = 24
  Placement = pos=(-92,-24,44) rot=(0,0,1;0rad)
  Width = 6
FEATURE [Part::Chamfer] Chamfer016
  Base = -> Box521
  Edges = 1 edges r=13.99: [Edge4]
FEATURE [Part::Compound] Compound531  label="stabilo_holdo_left_silo"
  Links = -> [Compound497,Chamfer016]
FEATURE [Part::Box] Box416  label="Krychle416"
  AttacherType = Attacher::AttachEngine3D
  Height = 26
  Length = 38
  Placement = pos=(-112,0,56) rot=(0,0,1;0rad)
  Width = 32
FEATURE [Part::Box] Box417  label="Krychle417"
  AttacherType = Attacher::AttachEngine3D
  Height = 20
  Length = 20
  Placement = pos=(-106,4,56) rot=(0,0,1;0rad)
  Width = 80
FEATURE [Part::Cut] Cut521
  Base = -> Box416
  Tool = -> Box417
FEATURE [Part::Box] Box418  label="Krychle418"
  AttacherType = Attacher::AttachEngine3D
  Height = 2
  Length = 6
  Placement = pos=(-112,4,60) rot=(0,0,1;0rad)
  Width = 6
FEATURE [Part::Box] Box419  label="Krychle419"
  AttacherType = Attacher::AttachEngine3D
  Height = 2
  Length = 6
  Placement = pos=(-112,22,60) rot=(0,0,1;0rad)
  Width = 6
FEATURE [Part::Box] Box420  label="Krychle420"
  AttacherType = Attacher::AttachEngine3D
  Height = 2
  Length = 6
  Placement = pos=(-86,4,60) rot=(0,0,1;0rad)
  Width = 6
FEATURE [Part::Box] Box421  label="Krychle421"
  AttacherType = Attacher::AttachEngine3D
  Height = 2
  Length = 6
  Placement = pos=(-86,22,60) rot=(0,0,1;0rad)
  Width = 6
FEATURE [Part::Compound] Compound488
  Links = -> [Box418,Box419,Box420,Box421]
FEATURE [Part::Cut] Cut392
  Base = -> Cut521
  Tool = -> Compound488
FEATURE [Part::Cylinder] Cylinder1759  label="Válec1759"
  Angle = 360
  AttacherType = Attacher::AttachEngine3D
  Height = 20
  Placement = pos=(-83,7,54) rot=(0,0,1;0rad)
  Radius = 1.5
FEATURE [Part::Cylinder] Cylinder875  label="Válec875"
  Angle = 360
  AttacherType = Attacher::AttachEngine3D
  Height = 20
  Placement = pos=(-83,25,54) rot=(0,0,1;0rad)
  Radius = 1.5
FEATURE [Part::Cylinder] Cylinder876  label="Válec876"
  Angle = 360
  AttacherType = Attacher::AttachEngine3D
  Height = 20
  Placement = pos=(-109,7,54) rot=(0,0,1;0rad)
  Radius = 1.5
FEATURE [Part::Cylinder] Cylinder877  label="Válec877"
  Angle = 360
  AttacherType = Attacher::AttachEngine3D
  Height = 20
  Placement = pos=(-109,25,54) rot=(0,0,1;0rad)
  Radius = 1.5
FEATURE [Part::Compound] Compound489
  Links = -> [Cylinder1759,Cylinder875,Cylinder876,Cylinder877]
FEATURE [Part::Cut] Cut393
  Base = -> Cut392
  Tool = -> Compound489
FEATURE [Part::Cylinder] Cylinder892  label="Válec892"
  Angle = 360
  AttacherType = Attacher::AttachEngine3D
  Height = 20
  Placement = pos=(-117,16,66) rot=(0,1,0;1.5708rad)
  Radius = 2.5
FEATURE [Part::Cut] Cut398
  Base = -> Cut393
  Tool = -> Cylinder892
FEATURE [Part::Cylinder] Cylinder893  label="Válec893"
  Angle = 360
  AttacherType = Attacher::AttachEngine3D
  Height = 3
  Placement = pos=(-112,16,66) rot=(0,1,0;1.5708rad)
  Radius = 5
FEATURE [Part::Box] Box423  label="Krychle423"
  AttacherType = Attacher::AttachEngine3D
  Height = 6
  Length = 51
  Placement = pos=(-112,-24,76) rot=(0,0,1;0rad)
  Width = 24
FEATURE [Part::Cut] Cut399
  Base = -> Cut398
  Tool = -> Cylinder893
FEATURE [Part::Chamfer] Chamfer002
  Base = -> Cut399
  Edges = 1 edges r=2: [Edge4]
FEATURE [Part::Cylinder] Cylinder894  label="Válec894"
  Angle = 360
  AttacherType = Attacher::AttachEngine3D
  Height = 10
  Placement = pos=(0,0,72) rot=(0,0,1;0rad)
  Radius = 74
FEATURE [Part::Cut] Cut400
  Base = -> Box423
  Tool = -> Cylinder894
FEATURE [Part::Box] Box424  label="Krychle424"
  AttacherType = Attacher::AttachEngine3D
  Height = 26
  Length = 50
  Placement = pos=(-112,-24,56) rot=(0,0,1;0rad)
  Width = 6
FEATURE [Part::Cylinder] Cylinder895  label="Válec895"
  Angle = 360
  AttacherType = Attacher::AttachEngine3D
  Height = 20
  Placement = pos=(-102,-10,66) rot=(0,0,1;0rad)
  Radius = 2.5
FEATURE [Part::Cylinder] Cylinder897  label="Válec897"
  Angle = 360
  AttacherType = Attacher::AttachEngine3D
  Height = 32
  Placement = pos=(0,0,50) rot=(0,0,1;0rad)
  Radius = 74
FEATURE [Part::Cut] Cut401
  Base = -> Box424
  Tool = -> Cylinder897
FEATURE [Part::Cylinder] Cylinder898  label="Válec898"
  Angle = 360
  AttacherType = Attacher::AttachEngine3D
  Height = 20
  Placement = pos=(-86,-10,66) rot=(0,0,1;0rad)
  Radius = 2.5
FEATURE [Part::Compound] Compound493
  Links = -> [Cylinder895,Cylinder898]
FEATURE [Part::Cut] Cut402
  Base = -> Cut400
  Tool = -> Compound493
FEATURE [Part::Chamfer] Chamfer057
  Base = -> Cut401
  Edges = 1 edges r=20: [Edge4]
FEATURE [Part::Compound] Compound494  label="stabilo_holdo_left1"
  Links = -> [Chamfer057,Cut402,Chamfer002]
FEATURE [Part::Mirroring] mirror  label="stabilo_holdo_right"
  Base = (0,0,0)
  Normal = (1,0,0)
  Placement = pos=(0,0,2) rot=(0,0,1;0rad)
  Source = -> Compound494
FEATURE [Part::Box] Box522  label="Krychle522"
  AttacherType = Attacher::AttachEngine3D
  Height = 14
  Length = 24
  Placement = pos=(68,-24,44) rot=(0,0,1;0rad)
  Width = 6
FEATURE [Part::Chamfer] Chamfer017
  Base = -> Box522
  Edges = 1 edges r=13.99: [Edge8]
FEATURE [Part::Compound] Compound532  label="stabilo_holdo_right_silo"
  Links = -> [Chamfer017,mirror]
FEATURE [Part::Cylinder] Cylinder961  label="Válec961"
  Angle = 360
  AttacherType = Attacher::AttachEngine3D
  Height = 20
  Placement = pos=(-102,-10,66) rot=(0,0,1;0rad)
  Radius = 2.5
FEATURE [Part::Cylinder] Cylinder962  label="Válec962"
  Angle = 360
  AttacherType = Attacher::AttachEngine3D
  Height = 10
  Placement = pos=(0,0,72) rot=(0,0,1;0rad)
  Radius = 74
FEATURE [Part::Box] Box476  label="Krychle476"
  AttacherType = Attacher::AttachEngine3D
  Height = 26
  Length = 50
  Placement = pos=(-112,-24,56) rot=(0,0,1;0rad)
  Width = 6
FEATURE [Part::Cylinder] Cylinder963  label="Válec963"
  Angle = 360
  AttacherType = Attacher::AttachEngine3D
  Height = 20
  Placement = pos=(-86,-10,66) rot=(0,0,1;0rad)
  Radius = 2.5
FEATURE [Part::Compound] Compound519
  Links = -> [Cylinder961,Cylinder963]
FEATURE [Part::Cylinder] Cylinder964  label="Válec964"
  Angle = 360
  AttacherType = Attacher::AttachEngine3D
  Height = 32
  Placement = pos=(0,0,50) rot=(0,0,1;0rad)
  Radius = 74
FEATURE [Part::Cut] Cut443
  Base = -> Box476
  Placement = pos=(0,0,0) rot=(0,0,1;1.5708rad)
  Tool = -> Cylinder964
FEATURE [Part::Box] Box477  label="Krychle477"
  AttacherType = Attacher::AttachEngine3D
  Height = 6
  Length = 51
  Placement = pos=(-112,-24,76) rot=(0,0,1;0rad)
  Width = 24
FEATURE [Part::Cylinder] Cylinder965  label="Válec965"
  Angle = 360
  AttacherType = Attacher::AttachEngine3D
  Height = 20
  Placement = pos=(-102,-10,66) rot=(0,0,1;0rad)
  Radius = 2.5
FEATURE [Part::Box] Box478  label="Krychle478"
  AttacherType = Attacher::AttachEngine3D
  Height = 26
  Length = 50
  Placement = pos=(-112,-24,56) rot=(0,0,1;0rad)
  Width = 6
FEATURE [Part::Cylinder] Cylinder966  label="Válec966"
  Angle = 360
  AttacherType = Attacher::AttachEngine3D
  Height = 32
  Placement = pos=(0,0,50) rot=(0,0,1;0rad)
  Radius = 74
FEATURE [Part::Cut] Cut445
  Base = -> Box477
  Tool = -> Cylinder962
FEATURE [Part::Cut] Cut444
  Base = -> Cut445
  Placement = pos=(0,0,0) rot=(0,0,1;1.5708rad)
  Tool = -> Compound519
FEATURE [Part::Compound] Compound520
  Links = -> [Cut443,Cut444]
FEATURE [Part::Cut] Cut446
  Base = -> Box478
  Placement = pos=(0,0,0) rot=(0,0,1;1.5708rad)
  Tool = -> Cylinder966
FEATURE [Part::Chamfer] Chamfer012
  Base = -> Compound520
  Edges = 1 edges r=20: [Edge4]
FEATURE [Part::Cylinder] Cylinder967  label="Válec967"
  Angle = 360
  AttacherType = Attacher::AttachEngine3D
  Height = 10
  Placement = pos=(0,0,72) rot=(0,0,1;0rad)
  Radius = 74
FEATURE [Part::Box] Box479  label="Krychle479"
  AttacherType = Attacher::AttachEngine3D
  Height = 6
  Length = 51
  Placement = pos=(-112,-24,76) rot=(0,0,1;0rad)
  Width = 24
FEATURE [Part::Cut] Cut447
  Base = -> Box479
  Tool = -> Cylinder967
FEATURE [Part::Cylinder] Cylinder968  label="Válec968"
  Angle = 360
  AttacherType = Attacher::AttachEngine3D
  Height = 20
  Placement = pos=(-86,-10,66) rot=(0,0,1;0rad)
  Radius = 2.5
FEATURE [Part::Compound] Compound522
  Links = -> [Cylinder965,Cylinder968]
FEATURE [Part::Cut] Cut448
  Base = -> Cut447
  Placement = pos=(0,0,0) rot=(0,0,1;1.5708rad)
  Tool = -> Compound522
FEATURE [Part::Compound] Compound521
  Links = -> [Cut446,Cut448]
FEATURE [Part::Mirroring] mirror003  label="Compound521 (mirrored)"
  Base = (0,0,0)
  Normal = (1,0,0)
  Source = -> Compound521
FEATURE [Part::Chamfer] Chamfer010
  Base = -> mirror003
  Edges = 1 edges r=20: [Edge4]
FEATURE [Part::Box] Box480  label="Krychle480"
  AttacherType = Attacher::AttachEngine3D
  Height = 26
  Length = 50
  Placement = pos=(3,-112,56) rot=(0,0,1;1.5708rad)
  Width = 6
FEATURE [Part::Cylinder] Cylinder969  label="Válec969"
  Angle = 360
  AttacherType = Attacher::AttachEngine3D
  Height = 40
  Placement = pos=(0,0,42) rot=(0,0,1;0rad)
  Radius = 74
FEATURE [Part::Box] Box481  label="Krychle481"
  AttacherType = Attacher::AttachEngine3D
  Height = 26
  Length = 8
  Placement = pos=(24,-78,56) rot=(0,0,1;1.5708rad)
  Width = 48
FEATURE [Part::Cylinder] Cylinder970  label="Válec970"
  Angle = 360
  AttacherType = Attacher::AttachEngine3D
  Height = 40
  Placement = pos=(0,0,42) rot=(0,0,1;0rad)
  Radius = 74
FEATURE [Part::Cut] Cut449
  Base = -> Box480
  Tool = -> Cylinder969
FEATURE [Part::Chamfer] Chamfer011
  Base = -> Cut449
  Edges = 1 edges r=20: [Edge4]
FEATURE [Part::Cut] Cut450
  Base = -> Box481
  Tool = -> Cylinder970
FEATURE [Part::Compound] Compound523  label="stabilo_front"
  Links = -> [Chamfer012,Chamfer011,Chamfer010,Cut450]
  Placement = pos=(0,0,2) rot=(0,0,1;0rad)
FEATURE [Part::Box] Box518  label="Krychle518"
  AttacherType = Attacher::AttachEngine3D
  Height = 14
  Length = 18
  Placement = pos=(3,-92,44) rot=(0,0,1;1.5708rad)
  Width = 6
FEATURE [Part::Chamfer] Chamfer013
  Base = -> Box518
  Edges = 1 edges r=13.99: [Edge4]
FEATURE [Part::Box] Box519  label="Krychle519"
  AttacherType = Attacher::AttachEngine3D
  Height = 14
  Length = 24
  Placement = pos=(3,-92,44) rot=(0,0,1;1.5708rad)
  Width = 6
FEATURE [Part::Chamfer] Chamfer014
  Base = -> Box519
  Edges = 1 edges r=13.99: [Edge4]
  Placement = pos=(-21,0,0) rot=(0,0,1;0rad)
FEATURE [Part::Box] Box520  label="Krychle520"
  AttacherType = Attacher::AttachEngine3D
  Height = 14
  Length = 24
  Placement = pos=(3,-92,44) rot=(0,0,1;1.5708rad)
  Width = 6
FEATURE [Part::Chamfer] Chamfer015
  Base = -> Box520
  Edges = 1 edges r=13.99: [Edge4]
  Placement = pos=(21,0,0) rot=(0,0,1;0rad)
FEATURE [Part::Compound] Compound533  label="stabilo_front_silo"
  Links = -> [Compound523,Chamfer013,Chamfer014,Chamfer015]
FEATURE [Part::Compound] Compound889  label="Base_turret-hole"
  Links = -> [Cut453,Tube036,Cut509,Cut520,Compound531,Compound532,Compound533]
FEATURE [Part::Box] Box711  label="Krychle711"
  AttacherType = Attacher::AttachEngine3D
  Height = 4
  Length = 28.8
  Placement = pos=(-14.4,10,24) rot=(0,0,1;0rad)
  Width = 2
FEATURE [Part::Compound] Compound890
  Links = -> [Box711]
  Placement = pos=(63.64,-63.64,38) rot=(0,0,1;3.92699rad)
FEATURE [Part::Cut] Cut522
  Base = -> Cut481
  Tool = -> Compound890
FEATURE [Part::Cylinder] Cylinder1760  label="Válec1760"
  Angle = 360
  AttacherType = Attacher::AttachEngine3D
  Height = 4
  Placement = pos=(63.64,-63.64,64) rot=(0,0,1;3.92699rad)
  Radius = 9
FEATURE [Part::Cut] Cut523
  Base = -> Cut522
  Tool = -> Cylinder1760
FEATURE [Part::Chamfer] Chamfer058  label="Base_encoder-washer"
  Base = -> Cut523
  Edges = 2 edges r=2: [Edge3,Edge31]
FEATURE [Mesh::Feature] Mesh007  label="Base_encoder-washer (Meshed)"
FEATURE [Mesh::Feature] Mesh  label="Base_turret-hole (Meshed)"
FEATURE [Part::FeaturePython] Tube040  label="Base_under-pulley_washer_A"  # WARN: FeaturePython — macro-defined, semantics opaque (R4)
  AttacherType = Attacher::AttachEngine3D
  Height = 4
  InnerRadius = 1.8
  OuterRadius = 3.8
FEATURE [Part::FeaturePython] Tube041  label="Base_under-pulley_washer_B"  # WARN: FeaturePython — macro-defined, semantics opaque (R4)
  AttacherType = Attacher::AttachEngine3D
  Height = 3
  InnerRadius = 1.8
  OuterRadius = 3.8
FEATURE [Mesh::Feature] Mesh009  label="Base_under-pulley_washer_A (Meshed)"
FEATURE [Mesh::Feature] Mesh010  label="Base_under-pulley_washer_B (Meshed)"
FEATURE [Part::FeaturePython] Tube042  label="Base_under-pulley_washer_C"  # WARN: FeaturePython — macro-defined, semantics opaque (R4)
  AttacherType = Attacher::AttachEngine3D
  Height = 5
  InnerRadius = 1.8
  OuterRadius = 3.8
FEATURE [Part::FeaturePython] Tube043  label="Base_under-pulley_washer_D"  # WARN: FeaturePython — macro-defined, semantics opaque (R4)
  AttacherType = Attacher::AttachEngine3D
  Height = 6
  InnerRadius = 1.8
  OuterRadius = 3.8
FEATURE [Mesh::Feature] Mesh011  label="Base_under-pulley_washer_C (Meshed)"
FEATURE [Mesh::Feature] Mesh012  label="Base_under-pulley_washer_D (Meshed)"
FEATURE [Part::FeaturePython] Tube044  label="ZKL-6017"  # WARN: FeaturePython — macro-defined, semantics opaque (R4)
  AttacherType = Attacher::AttachEngine3D
  Height = 22
  InnerRadius = 42.5
  OuterRadius = 65
  Placement = pos=(0,0,28) rot=(0,0,1;0rad)
FEATURE [Mesh::Feature] Mesh013  label="Base_encoder-uphold (Meshed)001"
FEATURE [Mesh::Feature] Mesh014  label="Base_encoder-bottomhold (Meshed)001"
FEATURE [Mesh::Feature] Mesh015  label="Base_encoder-sidehold (Meshed)001"
FEATURE [Mesh::Feature] Mesh016  label="Base_encoder-lowhold (Meshed)001"
FEATURE [Mesh::Feature] Mesh017  label="Base_encoder-tophold (Meshed)001"
FEATURE [Mesh::Feature] Mesh018  label="Base_turret-hole (Meshed)001"
FEATURE [Mesh::Feature] Mesh019  label="Base_encoder-washer (Meshed)001"
FEATURE [Mesh::Feature] Mesh001  label="Base_pulley-cover (Meshed)"
FEATURE [Mesh::Feature] Mesh002  label="Base_encoder-lowhold (Meshed)"
FEATURE [Mesh::Feature] Mesh003  label="Base_encoder-tophold (Meshed)"
FEATURE [Mesh::Feature] Mesh004  label="Base_encoder-uphold (Meshed)"
FEATURE [Mesh::Feature] Mesh005  label="Base_encoder-sidehold (Meshed)"
FEATURE [Mesh::Feature] Mesh006  label="Base_encoder-bottomhold (Meshed)"
FEATURE [Part::Cylinder] Cylinder882  label="Válec882"
  Angle = 360
  AttacherType = Attacher::AttachEngine3D
  Height = 3
  Placement = pos=(-96,16,50) rot=(0,0,1;0rad)
  Radius = 5
FEATURE [Part::Box] Box422  label="Krychle422"
  AttacherType = Attacher::AttachEngine3D
  Height = 6
  Length = 38
  Placement = pos=(-112,0,50) rot=(0,0,1;0rad)
  Width = 32
FEATURE [Part::Cylinder] Cylinder886  label="Válec886"
  Angle = 360
  AttacherType = Attacher::AttachEngine3D
  Height = 20
  Placement = pos=(-109,25,54) rot=(0,0,1;0rad)
  Radius = 1.5
FEATURE [Part::Cylinder] Cylinder885  label="Válec885"
  Angle = 360
  AttacherType = Attacher::AttachEngine3D
  Height = 20
  Placement = pos=(-109,7,54) rot=(0,0,1;0rad)
  Radius = 1.5
FEATURE [Part::Cylinder] Cylinder888  label="Válec888"
  Angle = 360
  AttacherType = Attacher::AttachEngine3D
  Height = 3
  Placement = pos=(-109,7,54) rot=(0,0,1;0rad)
  Radius = 3
FEATURE [Part::Cylinder] Cylinder887  label="Válec887"
  Angle = 360
  AttacherType = Attacher::AttachEngine3D
  Height = 3
  Placement = pos=(-83,25,54) rot=(0,0,1;0rad)
  Radius = 3
FEATURE [Part::Cylinder] Cylinder883  label="Válec883"
  Angle = 360
  AttacherType = Attacher::AttachEngine3D
  Height = 20
  Placement = pos=(-83,25,54) rot=(0,0,1;0rad)
  Radius = 1.5
FEATURE [Part::Cylinder] Cylinder884  label="Válec884"
  Angle = 360
  AttacherType = Attacher::AttachEngine3D
  Height = 20
  Placement = pos=(-83,7,54) rot=(0,0,1;0rad)
  Radius = 1.5
FEATURE [Part::Compound] Compound491
  Links = -> [Cylinder884,Cylinder883,Cylinder885,Cylinder886]
  Placement = pos=(0,0,-4) rot=(0,0,1;0rad)
FEATURE [Part::Cylinder] Cylinder890  label="Válec890"
  Angle = 360
  AttacherType = Attacher::AttachEngine3D
  Height = 3
  Placement = pos=(-109,25,54) rot=(0,0,1;0rad)
  Radius = 3
FEATURE [Part::Cylinder] Cylinder889  label="Válec889"
  Angle = 360
  AttacherType = Attacher::AttachEngine3D
  Height = 3
  Placement = pos=(-83,7,54) rot=(0,0,1;0rad)
  Radius = 3
FEATURE [Part::Compound] Compound492
  Links = -> [Cylinder889,Cylinder887,Cylinder888,Cylinder890]
  Placement = pos=(0,0,-4) rot=(0,0,1;0rad)
FEATURE [Part::Cut] Cut394
  Base = -> Box422
  Tool = -> Compound492
FEATURE [Part::Cut] Cut395
  Base = -> Cut394
  Tool = -> Compound491
FEATURE [Part::Cylinder] Cylinder891  label="Válec891"
  Angle = 360
  AttacherType = Attacher::AttachEngine3D
  Height = 20
  Placement = pos=(-96,16,50) rot=(0,0,1;0rad)
  Radius = 2.5
FEATURE [Part::Cut] Cut396
  Base = -> Cut395
  Tool = -> Cylinder891
FEATURE [Part::Cut] Cut397
  Base = -> Cut396
  Tool = -> Cylinder882
FEATURE [Part::Chamfer] Chamfer001  label="Base_stabil-cover-left"
  Base = -> Cut397
  Edges = 1 edges r=2: [Edge4]
FEATURE [Mesh::Feature] Mesh020  label="Base-stabil-cover-left (Meshed)"
FEATURE [Part::Cylinder] Cylinder910  label="Válec910"
  Angle = 360
  AttacherType = Attacher::AttachEngine3D
  Height = 20
  Placement = pos=(-109,7,54) rot=(0,0,1;0rad)
  Radius = 1.5
FEATURE [Part::Cylinder] Cylinder911  label="Válec911"
  Angle = 360
  AttacherType = Attacher::AttachEngine3D
  Height = 3
  Placement = pos=(-83,25,54) rot=(0,0,1;0rad)
  Radius = 3
FEATURE [Part::Cylinder] Cylinder912  label="Válec912"
  Angle = 360
  AttacherType = Attacher::AttachEngine3D
  Height = 20
  Placement = pos=(-83,7,54) rot=(0,0,1;0rad)
  Radius = 1.5
FEATURE [Part::Cylinder] Cylinder909  label="Válec909"
  Angle = 360
  AttacherType = Attacher::AttachEngine3D
  Height = 20
  Placement = pos=(-83,25,54) rot=(0,0,1;0rad)
  Radius = 1.5
FEATURE [Part::Cylinder] Cylinder913  label="Válec913"
  Angle = 360
  AttacherType = Attacher::AttachEngine3D
  Height = 20
  Placement = pos=(-96,16,50) rot=(0,0,1;0rad)
  Radius = 2.5
FEATURE [Part::Cylinder] Cylinder914  label="Válec914"
  Angle = 360
  AttacherType = Attacher::AttachEngine3D
  Height = 3
  Placement = pos=(-83,7,54) rot=(0,0,1;0rad)
  Radius = 3
FEATURE [Part::Cylinder] Cylinder916  label="Válec916"
  Angle = 360
  AttacherType = Attacher::AttachEngine3D
  Height = 20
  Placement = pos=(-109,25,54) rot=(0,0,1;0rad)
  Radius = 1.5
FEATURE [Part::Compound] Compound499
  Links = -> [Cylinder912,Cylinder909,Cylinder910,Cylinder916]
  Placement = pos=(0,0,-4) rot=(0,0,1;0rad)
FEATURE [Part::Cylinder] Cylinder917  label="Válec917"
  Angle = 360
  AttacherType = Attacher::AttachEngine3D
  Height = 3
  Placement = pos=(-109,7,54) rot=(0,0,1;0rad)
  Radius = 3
FEATURE [Part::Cylinder] Cylinder918  label="Válec918"
  Angle = 360
  AttacherType = Attacher::AttachEngine3D
  Height = 3
  Placement = pos=(-96,16,50) rot=(0,0,1;0rad)
  Radius = 5
FEATURE [Part::Cylinder] Cylinder915  label="Válec915"
  Angle = 360
  AttacherType = Attacher::AttachEngine3D
  Height = 3
  Placement = pos=(-109,25,54) rot=(0,0,1;0rad)
  Radius = 3
FEATURE [Part::Compound] Compound500
  Links = -> [Cylinder914,Cylinder911,Cylinder917,Cylinder915]
  Placement = pos=(0,0,-4) rot=(0,0,1;0rad)
FEATURE [Part::Box] Box433  label="Krychle433"
  AttacherType = Attacher::AttachEngine3D
  Height = 6
  Length = 38
  Placement = pos=(-112,0,50) rot=(0,0,1;0rad)
  Width = 32
FEATURE [Part::Cut] Cut411
  Base = -> Box433
  Tool = -> Compound500
FEATURE [Part::Cut] Cut414
  Base = -> Cut411
  Tool = -> Compound499
FEATURE [Part::Cut] Cut413
  Base = -> Cut414
  Tool = -> Cylinder913
FEATURE [Part::Cut] Cut412
  Base = -> Cut413
  Tool = -> Cylinder918
FEATURE [Part::Chamfer] Chamfer005  label="stabilo_cavo_left001"
  Base = -> Cut412
  Edges = 1 edges r=2: [Edge4]
FEATURE [Part::Mirroring] mirror001  label="Base_stabil-cover-right"
  Base = (0,0,0)
  Normal = (1,0,0)
  Source = -> Chamfer005
FEATURE [Mesh::Feature] Mesh021  label="Base-stabil-cover-right (Meshed)"
FEATURE [Mesh::Feature] Mesh022  label="Base_encoder-washer (Meshed)002"
FEATURE [Mesh::Feature] Mesh023  label="Base_encoder-uphold (Meshed)002"
FEATURE [Mesh::Feature] Mesh024  label="Base_encoder-bottomhold (Meshed)002"
FEATURE [Mesh::Feature] Mesh025  label="Base_encoder-sidehold (Meshed)002"
FEATURE [Mesh::Feature] Mesh026  label="Base_encoder-washer (Meshed)003"
